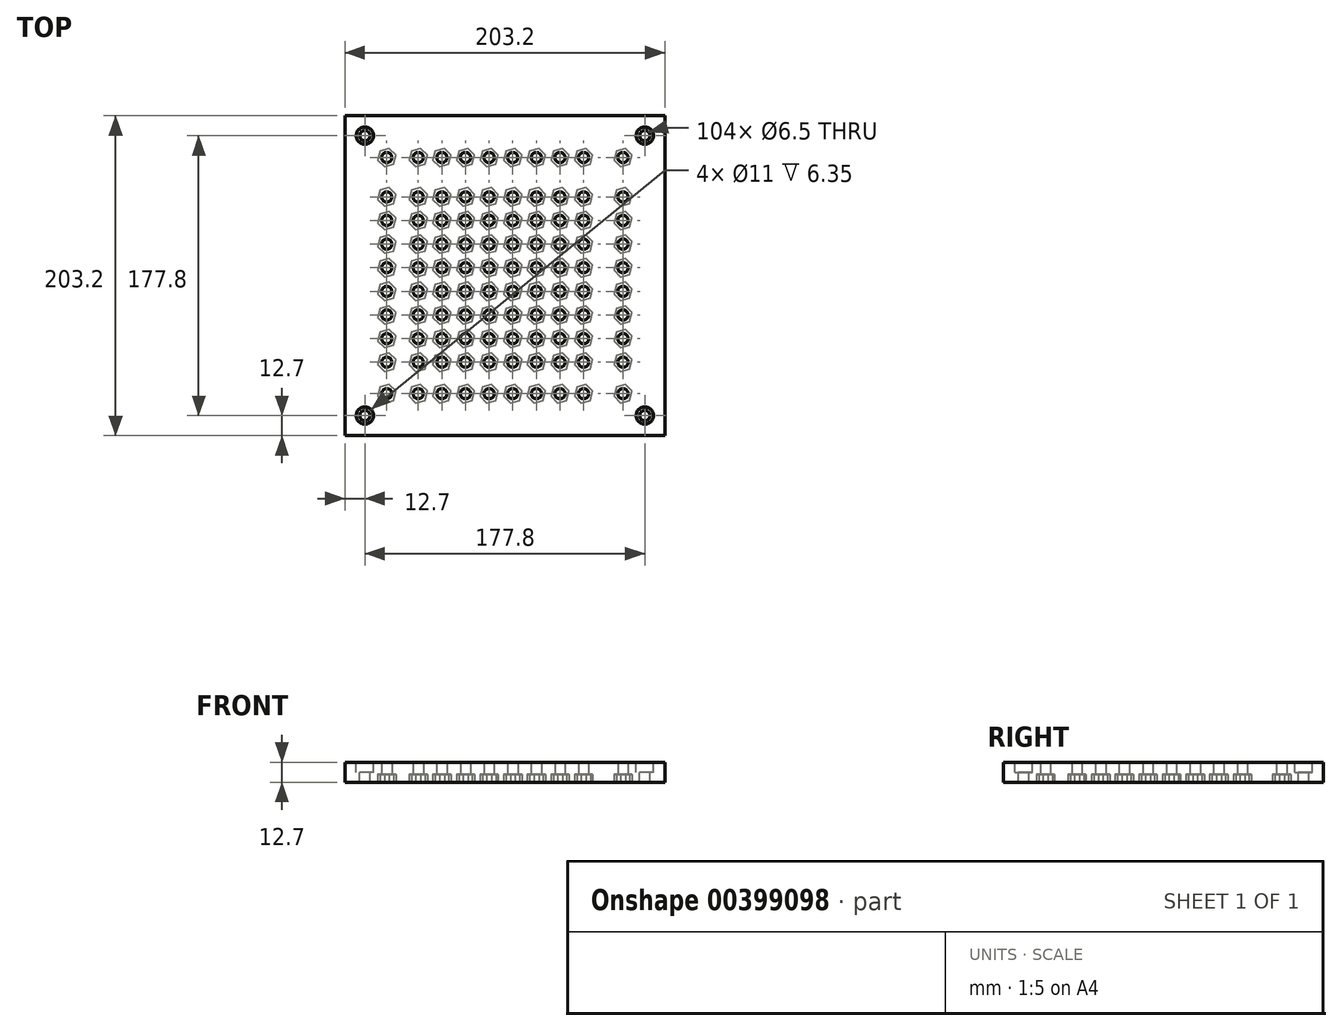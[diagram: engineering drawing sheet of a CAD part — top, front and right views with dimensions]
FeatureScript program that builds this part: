
annotation { "Feature Type Name" : "Feature", "Feature Type Description" : "" }
export const myFeature = defineFeature(function(context is Context, id is Id, definition is map)
    precondition{}
    {
        {
            assignVariable(context, id + "F0", {"name" : "M6NutThickness", "anyValue" : 5 * mm});
        }
        {
            var Q0;
            Q0=qCreatedBy(makeId("Top.planeOp"),FACE);
            var sketch = newSketch(context, id + "F1", { "sketchPlane" : qUnion([Q0])});
            skLineSegment(sketch, "E0.bottom", {"start": v(0, 0) * mm, "end": v(203.2, 0) * mm});
            skLineSegment(sketch, "E0.top", {"start": v(0, 203.2) * mm, "end": v(203.2, 203.2) * mm});
            skLineSegment(sketch, "E0.left", {"start": v(0, 0) * mm, "end": v(0, 203.2) * mm});
            skLineSegment(sketch, "E0.right", {"start": v(203.2, 0) * mm, "end": v(203.2, 203.2) * mm});
            skSolve(sketch);
        }
        {
            var Q0;
            Q0=makeQuery(id+"F1.imprint","IMPRINT",FACE,{"disambiguationData":[TD([[makeQuery(id+"F1.imprint","IMPRINT",EDGE,{"derivedFrom":sQuery(id+"F1.wireOp",EDGE,"E0.bottom")}),1.0]])]});
            extrude(context, id + "F2", {"entities" : qUnion([Q0]), "depth" : 12.7 * mm});
        }
        {
            var Q0;
            Q0=makeQuery(id+"F2.opExtrude","CAP_FACE",FACE,{"disambiguationData":[OSD([sQuery(id+"F1.wireOp",EDGE,"E0.bottom"),sQuery(id+"F1.wireOp",EDGE,"E0.top"),sQuery(id+"F1.wireOp",EDGE,"E0.left"),sQuery(id+"F1.wireOp",EDGE,"E0.right")])],"isStart":false});
            var sketch = newSketch(context, id + "F3", { "sketchPlane" : qUnion([Q0])});
            skCircle(sketch, "E1", {"center": v(12.7, 190.5) * mm, "radius": 5.5 * mm});
            skCircle(sketch, "E2", {"center": v(190.5, 190.5) * mm, "radius": 5.5 * mm});
            skCircle(sketch, "E3", {"center": v(190.5, 12.7) * mm, "radius": 5.5 * mm});
            skCircle(sketch, "E4", {"center": v(12.7, 12.7) * mm, "radius": 5.5 * mm});
            skCircle(sketch, "E5", {"center": v(12.7, 190.5) * mm, "radius": 3.25 * mm});
            skCircle(sketch, "E6", {"center": v(190.5, 190.5) * mm, "radius": 3.25 * mm});
            skCircle(sketch, "E7", {"center": v(190.5, 12.7) * mm, "radius": 3.25 * mm});
            skCircle(sketch, "E8", {"center": v(12.7, 12.7) * mm, "radius": 3.25 * mm});
            skSolve(sketch);
        }
        {
            var Q0;
            Q0=makeQuery(id+"F3.imprint","IMPRINT",FACE,{"disambiguationData":[TD([[makeQuery(id+"F3.imprint","IMPRINT",EDGE,{"derivedFrom":sQuery(id+"F3.wireOp",EDGE,"E1")}),1.0]])]});
            var Q1;
            Q1=makeQuery(id+"F3.imprint","IMPRINT",FACE,{"disambiguationData":[TD([[makeQuery(id+"F3.imprint","IMPRINT",EDGE,{"derivedFrom":sQuery(id+"F3.wireOp",EDGE,"E2")}),1.0]])]});
            var Q2;
            Q2=makeQuery(id+"F3.imprint","IMPRINT",FACE,{"disambiguationData":[TD([[makeQuery(id+"F3.imprint","IMPRINT",EDGE,{"derivedFrom":sQuery(id+"F3.wireOp",EDGE,"E3")}),1.0]])]});
            var Q3;
            Q3=makeQuery(id+"F3.imprint","IMPRINT",FACE,{"disambiguationData":[TD([[makeQuery(id+"F3.imprint","IMPRINT",EDGE,{"derivedFrom":sQuery(id+"F3.wireOp",EDGE,"E4")}),1.0]])]});
            var Q4;
            Q4=makeQuery(id+"F3.imprint","IMPRINT",FACE,{"disambiguationData":[TD([[makeQuery(id+"F3.imprint","IMPRINT",EDGE,{"derivedFrom":sQuery(id+"F3.wireOp",EDGE,"E5")}),1.0]])]});
            var Q5;
            Q5=makeQuery(id+"F3.imprint","IMPRINT",FACE,{"disambiguationData":[TD([[makeQuery(id+"F3.imprint","IMPRINT",EDGE,{"derivedFrom":sQuery(id+"F3.wireOp",EDGE,"ba32f473-7306-4966-8547-f8d374d792f3.0")}),-1.0]])]});
            var Q6;
            Q6=makeQuery(id+"F3.imprint","IMPRINT",FACE,{"disambiguationData":[TD([[makeQuery(id+"F3.imprint","IMPRINT",EDGE,{"derivedFrom":sQuery(id+"F3.wireOp",EDGE,"pHCyzxFQ-yNrH-yw88-MMIP-h8I6mzkWJt08")}),1.0]])]});
            var Q7;
            Q7=makeQuery(id+"F3.imprint","IMPRINT",FACE,{"disambiguationData":[TD([[makeQuery(id+"F3.imprint","IMPRINT",EDGE,{"derivedFrom":sQuery(id+"F3.wireOp",EDGE,"8c3efef8-5ac7-4a04-83c5-9b1e352e6b34")}),1.0]])]});
            var Q8;
            Q8=makeQuery(id+"F3.imprint","IMPRINT",FACE,{"disambiguationData":[TD([[makeQuery(id+"F3.imprint","IMPRINT",EDGE,{"derivedFrom":sQuery(id+"F3.wireOp",EDGE,"e6f48ea0-c1a9-460c-8d83-79fb5b6d435c.0")}),-1.0]])]});
            var Q9;
            Q9=makeQuery(id+"F3.imprint","IMPRINT",FACE,{"disambiguationData":[TD([[makeQuery(id+"F3.imprint","IMPRINT",EDGE,{"derivedFrom":sQuery(id+"F3.wireOp",EDGE,"E7")}),1.0]])]});
            var Q10;
            Q10=makeQuery(id+"F3.imprint","IMPRINT",FACE,{"disambiguationData":[TD([[makeQuery(id+"F3.imprint","IMPRINT",EDGE,{"derivedFrom":sQuery(id+"F3.wireOp",EDGE,"ca75a0d4-1ac4-49ba-8044-76483d581a22")}),1.0]])]});
            var Q11;
            Q11=makeQuery(id+"F3.imprint","IMPRINT",FACE,{"disambiguationData":[TD([[makeQuery(id+"F3.imprint","IMPRINT",EDGE,{"derivedFrom":sQuery(id+"F3.wireOp",EDGE,"484e9a5a-8a06-4af2-a13e-f69099c1e5a3.0")}),-1.0]])]});
            var Q12;
            Q12=makeQuery(id+"F3.imprint","IMPRINT",FACE,{"disambiguationData":[TD([[makeQuery(id+"F3.imprint","IMPRINT",EDGE,{"derivedFrom":sQuery(id+"F3.wireOp",EDGE,"0a7f3161-e935-40cb-8c32-bbe6e8a3d640.0")}),-1.0]])]});
            var Q13;
            Q13=makeQuery(id+"F3.imprint","IMPRINT",FACE,{"disambiguationData":[TD([[makeQuery(id+"F3.imprint","IMPRINT",EDGE,{"derivedFrom":sQuery(id+"F3.wireOp",EDGE,"f8818135-2c4b-4c98-9ffa-11e024e62321")}),1.0]])]});
            var Q14;
            Q14=makeQuery(id+"F3.imprint","IMPRINT",FACE,{"disambiguationData":[TD([[makeQuery(id+"F3.imprint","IMPRINT",EDGE,{"derivedFrom":sQuery(id+"F3.wireOp",EDGE,"3abde3a7-13fc-4790-a3ef-ddfa000d33fa")}),1.0]])]});
            var Q15;
            Q15=makeQuery(id+"F3.imprint","IMPRINT",FACE,{"disambiguationData":[TD([[makeQuery(id+"F3.imprint","IMPRINT",EDGE,{"derivedFrom":sQuery(id+"F3.wireOp",EDGE,"5478cdd5-5296-4cfe-a3e0-48035336e019.0")}),-1.0]])]});
            var Q16;
            Q16=makeQuery(id+"F3.imprint","IMPRINT",FACE,{"disambiguationData":[TD([[makeQuery(id+"F3.imprint","IMPRINT",EDGE,{"derivedFrom":sQuery(id+"F3.wireOp",EDGE,"bd25bac1-5707-4558-b08a-925dc677b274.0")}),-1.0]])]});
            var Q17;
            Q17=makeQuery(id+"F3.imprint","IMPRINT",FACE,{"disambiguationData":[TD([[makeQuery(id+"F3.imprint","IMPRINT",EDGE,{"derivedFrom":sQuery(id+"F3.wireOp",EDGE,"b3afb0ab-85e7-4117-a43b-624259399b40")}),1.0]])]});
            var Q18;
            Q18=makeQuery(id+"F3.imprint","IMPRINT",FACE,{"disambiguationData":[TD([[makeQuery(id+"F3.imprint","IMPRINT",EDGE,{"derivedFrom":sQuery(id+"F3.wireOp",EDGE,"E6")}),1.0]])]});
            var Q19;
            Q19=makeQuery(id+"F3.imprint","IMPRINT",FACE,{"disambiguationData":[TD([[makeQuery(id+"F3.imprint","IMPRINT",EDGE,{"derivedFrom":sQuery(id+"F3.wireOp",EDGE,"52d20c7e-8cc4-4a92-a8bc-447259732f1c")}),1.0]])]});
            var Q20;
            Q20=makeQuery(id+"F3.imprint","IMPRINT",FACE,{"disambiguationData":[TD([[makeQuery(id+"F3.imprint","IMPRINT",EDGE,{"derivedFrom":sQuery(id+"F3.wireOp",EDGE,"9f51e5bc-bef1-4550-8fb1-6146d32f1f4c.0")}),-1.0]])]});
            var Q21;
            Q21=makeQuery(id+"F3.imprint","IMPRINT",FACE,{"disambiguationData":[TD([[makeQuery(id+"F3.imprint","IMPRINT",EDGE,{"derivedFrom":sQuery(id+"F3.wireOp",EDGE,"a674802c-e204-4de5-9799-58b481744769")}),1.0]])]});
            var Q22;
            Q22=makeQuery(id+"F3.imprint","IMPRINT",FACE,{"disambiguationData":[TD([[makeQuery(id+"F3.imprint","IMPRINT",EDGE,{"derivedFrom":sQuery(id+"F3.wireOp",EDGE,"683618f0-5b4b-4870-9df9-abf6ab17f61a.0")}),-1.0]])]});
            var Q23;
            Q23=makeQuery(id+"F3.imprint","IMPRINT",FACE,{"disambiguationData":[TD([[makeQuery(id+"F3.imprint","IMPRINT",EDGE,{"derivedFrom":sQuery(id+"F3.wireOp",EDGE,"E8")}),1.0]])]});
            extrude(context, id + "F4", {"entities" : qUnion([Q0, Q1, Q2, Q3, Q4, Q5, Q6, Q7, Q8, Q9, Q10, Q11, Q12, Q13, Q14, Q15, Q16, Q17, Q18, Q19, Q20, Q21, Q22, Q23]), "operationType" : NewBodyOperationType.REMOVE, "oppositeDirection" : true, "depth" : 6.35 * mm});
        }
        {
            var Q0;
            Q0=makeQuery(id+"F3.imprint","IMPRINT",FACE,{"disambiguationData":[TD([[makeQuery(id+"F3.imprint","IMPRINT",EDGE,{"derivedFrom":sQuery(id+"F3.wireOp",EDGE,"E5")}),1.0]])]});
            var Q1;
            Q1=makeQuery(id+"F3.imprint","IMPRINT",FACE,{"disambiguationData":[TD([[makeQuery(id+"F3.imprint","IMPRINT",EDGE,{"derivedFrom":sQuery(id+"F3.wireOp",EDGE,"a674802c-e204-4de5-9799-58b481744769")}),1.0]])]});
            var Q2;
            Q2=makeQuery(id+"F3.imprint","IMPRINT",FACE,{"disambiguationData":[TD([[makeQuery(id+"F3.imprint","IMPRINT",EDGE,{"derivedFrom":sQuery(id+"F3.wireOp",EDGE,"52d20c7e-8cc4-4a92-a8bc-447259732f1c")}),1.0]])]});
            var Q3;
            Q3=makeQuery(id+"F3.imprint","IMPRINT",FACE,{"disambiguationData":[TD([[makeQuery(id+"F3.imprint","IMPRINT",EDGE,{"derivedFrom":sQuery(id+"F3.wireOp",EDGE,"E6")}),1.0]])]});
            var Q4;
            Q4=makeQuery(id+"F3.imprint","IMPRINT",FACE,{"disambiguationData":[TD([[makeQuery(id+"F3.imprint","IMPRINT",EDGE,{"derivedFrom":sQuery(id+"F3.wireOp",EDGE,"b3afb0ab-85e7-4117-a43b-624259399b40")}),1.0]])]});
            var Q5;
            Q5=makeQuery(id+"F3.imprint","IMPRINT",FACE,{"disambiguationData":[TD([[makeQuery(id+"F3.imprint","IMPRINT",EDGE,{"derivedFrom":sQuery(id+"F3.wireOp",EDGE,"3abde3a7-13fc-4790-a3ef-ddfa000d33fa")}),1.0]])]});
            var Q6;
            Q6=makeQuery(id+"F3.imprint","IMPRINT",FACE,{"disambiguationData":[TD([[makeQuery(id+"F3.imprint","IMPRINT",EDGE,{"derivedFrom":sQuery(id+"F3.wireOp",EDGE,"f8818135-2c4b-4c98-9ffa-11e024e62321")}),1.0]])]});
            var Q7;
            Q7=makeQuery(id+"F3.imprint","IMPRINT",FACE,{"disambiguationData":[TD([[makeQuery(id+"F3.imprint","IMPRINT",EDGE,{"derivedFrom":sQuery(id+"F3.wireOp",EDGE,"E7")}),1.0]])]});
            var Q8;
            Q8=makeQuery(id+"F3.imprint","IMPRINT",FACE,{"disambiguationData":[TD([[makeQuery(id+"F3.imprint","IMPRINT",EDGE,{"derivedFrom":sQuery(id+"F3.wireOp",EDGE,"ca75a0d4-1ac4-49ba-8044-76483d581a22")}),1.0]])]});
            var Q9;
            Q9=makeQuery(id+"F3.imprint","IMPRINT",FACE,{"disambiguationData":[TD([[makeQuery(id+"F3.imprint","IMPRINT",EDGE,{"derivedFrom":sQuery(id+"F3.wireOp",EDGE,"8c3efef8-5ac7-4a04-83c5-9b1e352e6b34")}),1.0]])]});
            var Q10;
            Q10=makeQuery(id+"F3.imprint","IMPRINT",FACE,{"disambiguationData":[TD([[makeQuery(id+"F3.imprint","IMPRINT",EDGE,{"derivedFrom":sQuery(id+"F3.wireOp",EDGE,"pHCyzxFQ-yNrH-yw88-MMIP-h8I6mzkWJt08")}),1.0]])]});
            var Q11;
            Q11=makeQuery(id+"F3.imprint","IMPRINT",FACE,{"disambiguationData":[TD([[makeQuery(id+"F3.imprint","IMPRINT",EDGE,{"derivedFrom":sQuery(id+"F3.wireOp",EDGE,"E8")}),1.0]])]});
            var Q12;
            Q12=makeQuery(id+"F2.opExtrude","CAP_FACE",FACE,{"disambiguationData":[OSD([sQuery(id+"F1.wireOp",EDGE,"E0.bottom"),sQuery(id+"F1.wireOp",EDGE,"E0.top"),sQuery(id+"F1.wireOp",EDGE,"E0.left"),sQuery(id+"F1.wireOp",EDGE,"E0.right")])],"isStart":true});
            extrude(context, id + "F5", {"entities" : qUnion([Q0, Q1, Q2, Q3, Q4, Q5, Q6, Q7, Q8, Q9, Q10, Q11]), "operationType" : NewBodyOperationType.REMOVE, "endBound" : BoundingType.THROUGH_ALL, "oppositeDirection" : true, "endBoundEntityFace" : qUnion([Q12]), "depth" : 25 * mm});
        }
        {
            var Q0;
            Q0=makeQuery(id+"F2.opExtrude","CAP_FACE",FACE,{"disambiguationData":[OSD([sQuery(id+"F1.wireOp",EDGE,"E0.bottom"),sQuery(id+"F1.wireOp",EDGE,"E0.top"),sQuery(id+"F1.wireOp",EDGE,"E0.left"),sQuery(id+"F1.wireOp",EDGE,"E0.right")])],"isStart":true});
            var sketch = newSketch(context, id + "F6", { "sketchPlane" : qUnion([Q0])});
            skCircle(sketch, "E9.cCircle", {"center": v(26.6, -26.6) * mm, "radius": 5.2 * mm, "construction": true});
            skLineSegment(sketch, "E9.0", {"start": v(25.05, -20.8) * mm, "end": v(30.85, -22.35) * mm});
            skLineSegment(sketch, "E9.1", {"start": v(30.85, -22.35) * mm, "end": v(32.4, -28.15) * mm});
            skLineSegment(sketch, "E9.2", {"start": v(32.4, -28.15) * mm, "end": v(28.15, -32.4) * mm});
            skLineSegment(sketch, "E9.3", {"start": v(28.15, -32.4) * mm, "end": v(22.35, -30.85) * mm});
            skLineSegment(sketch, "E9.4", {"start": v(22.35, -30.85) * mm, "end": v(20.8, -25.05) * mm});
            skLineSegment(sketch, "E9.5", {"start": v(20.8, -25.05) * mm, "end": v(25.05, -20.8) * mm});
            skPoint(sketch, "E9.0.midPoint", {"position": v(27.95, -21.58) * mm});
            skLineSegment(sketch, "E10", {"start": v(27.95, -21.58) * mm, "end": v(26.6, -26.6) * mm, "construction": true});
            skLineSegment(sketch, "E11", {"start": v(26.6, -21.4) * mm, "end": v(26.6, -26.6) * mm, "construction": true});
            skCircle(sketch, "E12", {"center": v(26.6, -26.6) * mm, "radius": 3.25 * mm});
            skCircle(sketch, "E13.cCircle", {"center": v(46.6, -26.6) * mm, "radius": 5.2 * mm, "construction": true});
            skLineSegment(sketch, "E13.0", {"start": v(45.05, -20.8) * mm, "end": v(50.85, -22.35) * mm});
            skLineSegment(sketch, "E13.1", {"start": v(50.85, -22.35) * mm, "end": v(52.4, -28.15) * mm});
            skLineSegment(sketch, "E13.2", {"start": v(52.4, -28.15) * mm, "end": v(48.15, -32.4) * mm});
            skLineSegment(sketch, "E13.3", {"start": v(48.15, -32.4) * mm, "end": v(42.35, -30.85) * mm});
            skLineSegment(sketch, "E13.4", {"start": v(42.35, -30.85) * mm, "end": v(40.8, -25.05) * mm});
            skLineSegment(sketch, "E13.5", {"start": v(40.8, -25.05) * mm, "end": v(45.05, -20.8) * mm});
            skPoint(sketch, "E13.0.midPoint", {"position": v(47.95, -21.58) * mm});
            skLineSegment(sketch, "E14", {"start": v(47.95, -21.58) * mm, "end": v(46.6, -26.6) * mm, "construction": true});
            skLineSegment(sketch, "E15", {"start": v(46.6, -21.4) * mm, "end": v(46.6, -26.6) * mm, "construction": true});
            skCircle(sketch, "E16", {"center": v(46.6, -26.6) * mm, "radius": 3.25 * mm});
            skCircle(sketch, "E17.cCircle", {"center": v(61.6, -26.6) * mm, "radius": 5.2 * mm, "construction": true});
            skLineSegment(sketch, "E17.0", {"start": v(60.05, -20.8) * mm, "end": v(65.85, -22.35) * mm});
            skLineSegment(sketch, "E17.1", {"start": v(65.85, -22.35) * mm, "end": v(67.4, -28.15) * mm});
            skLineSegment(sketch, "E17.2", {"start": v(67.4, -28.15) * mm, "end": v(63.15, -32.4) * mm});
            skLineSegment(sketch, "E17.3", {"start": v(63.15, -32.4) * mm, "end": v(57.35, -30.85) * mm});
            skLineSegment(sketch, "E17.4", {"start": v(57.35, -30.85) * mm, "end": v(55.8, -25.05) * mm});
            skLineSegment(sketch, "E17.5", {"start": v(55.8, -25.05) * mm, "end": v(60.05, -20.8) * mm});
            skPoint(sketch, "E17.0.midPoint", {"position": v(62.95, -21.58) * mm});
            skLineSegment(sketch, "E18", {"start": v(62.95, -21.58) * mm, "end": v(61.6, -26.6) * mm, "construction": true});
            skLineSegment(sketch, "E19", {"start": v(61.6, -21.4) * mm, "end": v(61.6, -26.6) * mm, "construction": true});
            skCircle(sketch, "E20", {"center": v(61.6, -26.6) * mm, "radius": 3.25 * mm});
            skCircle(sketch, "E21.cCircle", {"center": v(76.6, -26.6) * mm, "radius": 5.2 * mm, "construction": true});
            skLineSegment(sketch, "E21.0", {"start": v(75.05, -20.8) * mm, "end": v(80.85, -22.35) * mm});
            skLineSegment(sketch, "E21.1", {"start": v(80.85, -22.35) * mm, "end": v(82.4, -28.15) * mm});
            skLineSegment(sketch, "E21.2", {"start": v(82.4, -28.15) * mm, "end": v(78.15, -32.4) * mm});
            skLineSegment(sketch, "E21.3", {"start": v(78.15, -32.4) * mm, "end": v(72.35, -30.85) * mm});
            skLineSegment(sketch, "E21.4", {"start": v(72.35, -30.85) * mm, "end": v(70.8, -25.05) * mm});
            skLineSegment(sketch, "E21.5", {"start": v(70.8, -25.05) * mm, "end": v(75.05, -20.8) * mm});
            skPoint(sketch, "E21.0.midPoint", {"position": v(77.95, -21.58) * mm});
            skLineSegment(sketch, "E22", {"start": v(77.95, -21.58) * mm, "end": v(76.6, -26.6) * mm, "construction": true});
            skLineSegment(sketch, "E23", {"start": v(76.6, -21.4) * mm, "end": v(76.6, -26.6) * mm, "construction": true});
            skCircle(sketch, "E24", {"center": v(76.6, -26.6) * mm, "radius": 3.25 * mm});
            skCircle(sketch, "E25.cCircle", {"center": v(91.6, -26.6) * mm, "radius": 5.2 * mm, "construction": true});
            skLineSegment(sketch, "E25.0", {"start": v(90.05, -20.8) * mm, "end": v(95.85, -22.35) * mm});
            skLineSegment(sketch, "E25.1", {"start": v(95.85, -22.35) * mm, "end": v(97.4, -28.15) * mm});
            skLineSegment(sketch, "E25.2", {"start": v(97.4, -28.15) * mm, "end": v(93.15, -32.4) * mm});
            skLineSegment(sketch, "E25.3", {"start": v(93.15, -32.4) * mm, "end": v(87.35, -30.85) * mm});
            skLineSegment(sketch, "E25.4", {"start": v(87.35, -30.85) * mm, "end": v(85.8, -25.05) * mm});
            skLineSegment(sketch, "E25.5", {"start": v(85.8, -25.05) * mm, "end": v(90.05, -20.8) * mm});
            skPoint(sketch, "E25.0.midPoint", {"position": v(92.95, -21.58) * mm});
            skLineSegment(sketch, "E26", {"start": v(92.95, -21.58) * mm, "end": v(91.6, -26.6) * mm, "construction": true});
            skLineSegment(sketch, "E27", {"start": v(91.6, -21.4) * mm, "end": v(91.6, -26.6) * mm, "construction": true});
            skCircle(sketch, "E28", {"center": v(91.6, -26.6) * mm, "radius": 3.25 * mm});
            skCircle(sketch, "E29.cCircle", {"center": v(106.6, -26.6) * mm, "radius": 5.2 * mm, "construction": true});
            skLineSegment(sketch, "E29.0", {"start": v(105.05, -20.8) * mm, "end": v(110.85, -22.35) * mm});
            skLineSegment(sketch, "E29.1", {"start": v(110.85, -22.35) * mm, "end": v(112.4, -28.15) * mm});
            skLineSegment(sketch, "E29.2", {"start": v(112.4, -28.15) * mm, "end": v(108.15, -32.4) * mm});
            skLineSegment(sketch, "E29.3", {"start": v(108.15, -32.4) * mm, "end": v(102.35, -30.85) * mm});
            skLineSegment(sketch, "E29.4", {"start": v(102.35, -30.85) * mm, "end": v(100.8, -25.05) * mm});
            skLineSegment(sketch, "E29.5", {"start": v(100.8, -25.05) * mm, "end": v(105.05, -20.8) * mm});
            skPoint(sketch, "E29.0.midPoint", {"position": v(107.95, -21.58) * mm});
            skLineSegment(sketch, "E30", {"start": v(107.95, -21.58) * mm, "end": v(106.6, -26.6) * mm, "construction": true});
            skLineSegment(sketch, "E31", {"start": v(106.6, -21.4) * mm, "end": v(106.6, -26.6) * mm, "construction": true});
            skCircle(sketch, "E32", {"center": v(106.6, -26.6) * mm, "radius": 3.25 * mm});
            skCircle(sketch, "E33.cCircle", {"center": v(121.6, -26.6) * mm, "radius": 5.2 * mm, "construction": true});
            skLineSegment(sketch, "E33.0", {"start": v(120.05, -20.8) * mm, "end": v(125.85, -22.35) * mm});
            skLineSegment(sketch, "E33.1", {"start": v(125.85, -22.35) * mm, "end": v(127.4, -28.15) * mm});
            skLineSegment(sketch, "E33.2", {"start": v(127.4, -28.15) * mm, "end": v(123.15, -32.4) * mm});
            skLineSegment(sketch, "E33.3", {"start": v(123.15, -32.4) * mm, "end": v(117.35, -30.85) * mm});
            skLineSegment(sketch, "E33.4", {"start": v(117.35, -30.85) * mm, "end": v(115.8, -25.05) * mm});
            skLineSegment(sketch, "E33.5", {"start": v(115.8, -25.05) * mm, "end": v(120.05, -20.8) * mm});
            skPoint(sketch, "E33.0.midPoint", {"position": v(122.95, -21.58) * mm});
            skLineSegment(sketch, "E34", {"start": v(122.95, -21.58) * mm, "end": v(121.6, -26.6) * mm, "construction": true});
            skLineSegment(sketch, "E35", {"start": v(121.6, -21.4) * mm, "end": v(121.6, -26.6) * mm, "construction": true});
            skCircle(sketch, "E36", {"center": v(121.6, -26.6) * mm, "radius": 3.25 * mm});
            skCircle(sketch, "E37.cCircle", {"center": v(136.6, -26.6) * mm, "radius": 5.2 * mm, "construction": true});
            skLineSegment(sketch, "E37.0", {"start": v(135.05, -20.8) * mm, "end": v(140.85, -22.35) * mm});
            skLineSegment(sketch, "E37.1", {"start": v(140.85, -22.35) * mm, "end": v(142.4, -28.15) * mm});
            skLineSegment(sketch, "E37.2", {"start": v(142.4, -28.15) * mm, "end": v(138.15, -32.4) * mm});
            skLineSegment(sketch, "E37.3", {"start": v(138.15, -32.4) * mm, "end": v(132.35, -30.85) * mm});
            skLineSegment(sketch, "E37.4", {"start": v(132.35, -30.85) * mm, "end": v(130.8, -25.05) * mm});
            skLineSegment(sketch, "E37.5", {"start": v(130.8, -25.05) * mm, "end": v(135.05, -20.8) * mm});
            skPoint(sketch, "E37.0.midPoint", {"position": v(137.95, -21.58) * mm});
            skLineSegment(sketch, "E38", {"start": v(137.95, -21.58) * mm, "end": v(136.6, -26.6) * mm, "construction": true});
            skLineSegment(sketch, "E39", {"start": v(136.6, -21.4) * mm, "end": v(136.6, -26.6) * mm, "construction": true});
            skCircle(sketch, "E40", {"center": v(136.6, -26.6) * mm, "radius": 3.25 * mm});
            skCircle(sketch, "E41.cCircle", {"center": v(151.6, -26.6) * mm, "radius": 5.2 * mm, "construction": true});
            skLineSegment(sketch, "E41.0", {"start": v(150.05, -20.8) * mm, "end": v(155.85, -22.35) * mm});
            skLineSegment(sketch, "E41.1", {"start": v(155.85, -22.35) * mm, "end": v(157.4, -28.15) * mm});
            skLineSegment(sketch, "E41.2", {"start": v(157.4, -28.15) * mm, "end": v(153.15, -32.4) * mm});
            skLineSegment(sketch, "E41.3", {"start": v(153.15, -32.4) * mm, "end": v(147.35, -30.85) * mm});
            skLineSegment(sketch, "E41.4", {"start": v(147.35, -30.85) * mm, "end": v(145.8, -25.05) * mm});
            skLineSegment(sketch, "E41.5", {"start": v(145.8, -25.05) * mm, "end": v(150.05, -20.8) * mm});
            skPoint(sketch, "E41.0.midPoint", {"position": v(152.95, -21.58) * mm});
            skLineSegment(sketch, "E42", {"start": v(152.95, -21.58) * mm, "end": v(151.6, -26.6) * mm, "construction": true});
            skLineSegment(sketch, "E43", {"start": v(151.6, -21.4) * mm, "end": v(151.6, -26.6) * mm, "construction": true});
            skCircle(sketch, "E44", {"center": v(151.6, -26.6) * mm, "radius": 3.25 * mm});
            skCircle(sketch, "E45.cCircle", {"center": v(176.6, -26.6) * mm, "radius": 5.2 * mm, "construction": true});
            skLineSegment(sketch, "E45.0", {"start": v(175.05, -20.8) * mm, "end": v(180.85, -22.35) * mm});
            skLineSegment(sketch, "E45.1", {"start": v(180.85, -22.35) * mm, "end": v(182.4, -28.15) * mm});
            skLineSegment(sketch, "E45.2", {"start": v(182.4, -28.15) * mm, "end": v(178.15, -32.4) * mm});
            skLineSegment(sketch, "E45.3", {"start": v(178.15, -32.4) * mm, "end": v(172.35, -30.85) * mm});
            skLineSegment(sketch, "E45.4", {"start": v(172.35, -30.85) * mm, "end": v(170.8, -25.05) * mm});
            skLineSegment(sketch, "E45.5", {"start": v(170.8, -25.05) * mm, "end": v(175.05, -20.8) * mm});
            skPoint(sketch, "E45.0.midPoint", {"position": v(177.95, -21.58) * mm});
            skLineSegment(sketch, "E46", {"start": v(177.95, -21.58) * mm, "end": v(176.6, -26.6) * mm, "construction": true});
            skLineSegment(sketch, "E47", {"start": v(176.6, -21.4) * mm, "end": v(176.6, -26.6) * mm, "construction": true});
            skCircle(sketch, "E48", {"center": v(176.6, -26.6) * mm, "radius": 3.25 * mm});
            skCircle(sketch, "E49.cCircle", {"center": v(26.6, -46.6) * mm, "radius": 5.2 * mm, "construction": true});
            skLineSegment(sketch, "E49.0", {"start": v(25.05, -40.8) * mm, "end": v(30.85, -42.35) * mm});
            skLineSegment(sketch, "E49.1", {"start": v(30.85, -42.35) * mm, "end": v(32.4, -48.15) * mm});
            skLineSegment(sketch, "E49.2", {"start": v(32.4, -48.15) * mm, "end": v(28.15, -52.4) * mm});
            skLineSegment(sketch, "E49.3", {"start": v(28.15, -52.4) * mm, "end": v(22.35, -50.85) * mm});
            skLineSegment(sketch, "E49.4", {"start": v(22.35, -50.85) * mm, "end": v(20.8, -45.05) * mm});
            skLineSegment(sketch, "E49.5", {"start": v(20.8, -45.05) * mm, "end": v(25.05, -40.8) * mm});
            skPoint(sketch, "E49.0.midPoint", {"position": v(27.95, -41.58) * mm});
            skLineSegment(sketch, "E50", {"start": v(27.95, -41.58) * mm, "end": v(26.6, -46.6) * mm, "construction": true});
            skLineSegment(sketch, "E51", {"start": v(26.6, -41.4) * mm, "end": v(26.6, -46.6) * mm, "construction": true});
            skCircle(sketch, "E52", {"center": v(26.6, -46.6) * mm, "radius": 3.25 * mm});
            skCircle(sketch, "E53.cCircle", {"center": v(46.6, -46.6) * mm, "radius": 5.2 * mm, "construction": true});
            skLineSegment(sketch, "E53.0", {"start": v(45.05, -40.8) * mm, "end": v(50.85, -42.35) * mm});
            skLineSegment(sketch, "E53.1", {"start": v(50.85, -42.35) * mm, "end": v(52.4, -48.15) * mm});
            skLineSegment(sketch, "E53.2", {"start": v(52.4, -48.15) * mm, "end": v(48.15, -52.4) * mm});
            skLineSegment(sketch, "E53.3", {"start": v(48.15, -52.4) * mm, "end": v(42.35, -50.85) * mm});
            skLineSegment(sketch, "E53.4", {"start": v(42.35, -50.85) * mm, "end": v(40.8, -45.05) * mm});
            skLineSegment(sketch, "E53.5", {"start": v(40.8, -45.05) * mm, "end": v(45.05, -40.8) * mm});
            skPoint(sketch, "E53.0.midPoint", {"position": v(47.95, -41.58) * mm});
            skLineSegment(sketch, "E54", {"start": v(47.95, -41.58) * mm, "end": v(46.6, -46.6) * mm, "construction": true});
            skLineSegment(sketch, "E55", {"start": v(46.6, -41.4) * mm, "end": v(46.6, -46.6) * mm, "construction": true});
            skCircle(sketch, "E56", {"center": v(46.6, -46.6) * mm, "radius": 3.25 * mm});
            skCircle(sketch, "E57.cCircle", {"center": v(61.6, -46.6) * mm, "radius": 5.2 * mm, "construction": true});
            skLineSegment(sketch, "E57.0", {"start": v(60.05, -40.8) * mm, "end": v(65.85, -42.35) * mm});
            skLineSegment(sketch, "E57.1", {"start": v(65.85, -42.35) * mm, "end": v(67.4, -48.15) * mm});
            skLineSegment(sketch, "E57.2", {"start": v(67.4, -48.15) * mm, "end": v(63.15, -52.4) * mm});
            skLineSegment(sketch, "E57.3", {"start": v(63.15, -52.4) * mm, "end": v(57.35, -50.85) * mm});
            skLineSegment(sketch, "E57.4", {"start": v(57.35, -50.85) * mm, "end": v(55.8, -45.05) * mm});
            skLineSegment(sketch, "E57.5", {"start": v(55.8, -45.05) * mm, "end": v(60.05, -40.8) * mm});
            skPoint(sketch, "E57.0.midPoint", {"position": v(62.95, -41.58) * mm});
            skLineSegment(sketch, "E58", {"start": v(62.95, -41.58) * mm, "end": v(61.6, -46.6) * mm, "construction": true});
            skLineSegment(sketch, "E59", {"start": v(61.6, -41.4) * mm, "end": v(61.6, -46.6) * mm, "construction": true});
            skCircle(sketch, "E60", {"center": v(61.6, -46.6) * mm, "radius": 3.25 * mm});
            skCircle(sketch, "E61.cCircle", {"center": v(76.6, -46.6) * mm, "radius": 5.2 * mm, "construction": true});
            skLineSegment(sketch, "E61.0", {"start": v(75.05, -40.8) * mm, "end": v(80.85, -42.35) * mm});
            skLineSegment(sketch, "E61.1", {"start": v(80.85, -42.35) * mm, "end": v(82.4, -48.15) * mm});
            skLineSegment(sketch, "E61.2", {"start": v(82.4, -48.15) * mm, "end": v(78.15, -52.4) * mm});
            skLineSegment(sketch, "E61.3", {"start": v(78.15, -52.4) * mm, "end": v(72.35, -50.85) * mm});
            skLineSegment(sketch, "E61.4", {"start": v(72.35, -50.85) * mm, "end": v(70.8, -45.05) * mm});
            skLineSegment(sketch, "E61.5", {"start": v(70.8, -45.05) * mm, "end": v(75.05, -40.8) * mm});
            skPoint(sketch, "E61.0.midPoint", {"position": v(77.95, -41.58) * mm});
            skLineSegment(sketch, "E62", {"start": v(77.95, -41.58) * mm, "end": v(76.6, -46.6) * mm, "construction": true});
            skLineSegment(sketch, "E63", {"start": v(76.6, -41.4) * mm, "end": v(76.6, -46.6) * mm, "construction": true});
            skCircle(sketch, "E64", {"center": v(76.6, -46.6) * mm, "radius": 3.25 * mm});
            skCircle(sketch, "E65.cCircle", {"center": v(91.6, -46.6) * mm, "radius": 5.2 * mm, "construction": true});
            skLineSegment(sketch, "E65.0", {"start": v(90.05, -40.8) * mm, "end": v(95.85, -42.35) * mm});
            skLineSegment(sketch, "E65.1", {"start": v(95.85, -42.35) * mm, "end": v(97.4, -48.15) * mm});
            skLineSegment(sketch, "E65.2", {"start": v(97.4, -48.15) * mm, "end": v(93.15, -52.4) * mm});
            skLineSegment(sketch, "E65.3", {"start": v(93.15, -52.4) * mm, "end": v(87.35, -50.85) * mm});
            skLineSegment(sketch, "E65.4", {"start": v(87.35, -50.85) * mm, "end": v(85.8, -45.05) * mm});
            skLineSegment(sketch, "E65.5", {"start": v(85.8, -45.05) * mm, "end": v(90.05, -40.8) * mm});
            skPoint(sketch, "E65.0.midPoint", {"position": v(92.95, -41.58) * mm});
            skLineSegment(sketch, "E66", {"start": v(92.95, -41.58) * mm, "end": v(91.6, -46.6) * mm, "construction": true});
            skLineSegment(sketch, "E67", {"start": v(91.6, -41.4) * mm, "end": v(91.6, -46.6) * mm, "construction": true});
            skCircle(sketch, "E68", {"center": v(91.6, -46.6) * mm, "radius": 3.25 * mm});
            skCircle(sketch, "E69.cCircle", {"center": v(106.6, -46.6) * mm, "radius": 5.2 * mm, "construction": true});
            skLineSegment(sketch, "E69.0", {"start": v(105.05, -40.8) * mm, "end": v(110.85, -42.35) * mm});
            skLineSegment(sketch, "E69.1", {"start": v(110.85, -42.35) * mm, "end": v(112.4, -48.15) * mm});
            skLineSegment(sketch, "E69.2", {"start": v(112.4, -48.15) * mm, "end": v(108.15, -52.4) * mm});
            skLineSegment(sketch, "E69.3", {"start": v(108.15, -52.4) * mm, "end": v(102.35, -50.85) * mm});
            skLineSegment(sketch, "E69.4", {"start": v(102.35, -50.85) * mm, "end": v(100.8, -45.05) * mm});
            skLineSegment(sketch, "E69.5", {"start": v(100.8, -45.05) * mm, "end": v(105.05, -40.8) * mm});
            skPoint(sketch, "E69.0.midPoint", {"position": v(107.95, -41.58) * mm});
            skLineSegment(sketch, "E70", {"start": v(107.95, -41.58) * mm, "end": v(106.6, -46.6) * mm, "construction": true});
            skLineSegment(sketch, "E71", {"start": v(106.6, -41.4) * mm, "end": v(106.6, -46.6) * mm, "construction": true});
            skCircle(sketch, "E72", {"center": v(106.6, -46.6) * mm, "radius": 3.25 * mm});
            skCircle(sketch, "E73.cCircle", {"center": v(121.6, -46.6) * mm, "radius": 5.2 * mm, "construction": true});
            skLineSegment(sketch, "E73.0", {"start": v(120.05, -40.8) * mm, "end": v(125.85, -42.35) * mm});
            skLineSegment(sketch, "E73.1", {"start": v(125.85, -42.35) * mm, "end": v(127.4, -48.15) * mm});
            skLineSegment(sketch, "E73.2", {"start": v(127.4, -48.15) * mm, "end": v(123.15, -52.4) * mm});
            skLineSegment(sketch, "E73.3", {"start": v(123.15, -52.4) * mm, "end": v(117.35, -50.85) * mm});
            skLineSegment(sketch, "E73.4", {"start": v(117.35, -50.85) * mm, "end": v(115.8, -45.05) * mm});
            skLineSegment(sketch, "E73.5", {"start": v(115.8, -45.05) * mm, "end": v(120.05, -40.8) * mm});
            skPoint(sketch, "E73.0.midPoint", {"position": v(122.95, -41.58) * mm});
            skLineSegment(sketch, "E74", {"start": v(122.95, -41.58) * mm, "end": v(121.6, -46.6) * mm, "construction": true});
            skLineSegment(sketch, "E75", {"start": v(121.6, -41.4) * mm, "end": v(121.6, -46.6) * mm, "construction": true});
            skCircle(sketch, "E76", {"center": v(121.6, -46.6) * mm, "radius": 3.25 * mm});
            skCircle(sketch, "E77.cCircle", {"center": v(136.6, -46.6) * mm, "radius": 5.2 * mm, "construction": true});
            skLineSegment(sketch, "E77.0", {"start": v(135.05, -40.8) * mm, "end": v(140.85, -42.35) * mm});
            skLineSegment(sketch, "E77.1", {"start": v(140.85, -42.35) * mm, "end": v(142.4, -48.15) * mm});
            skLineSegment(sketch, "E77.2", {"start": v(142.4, -48.15) * mm, "end": v(138.15, -52.4) * mm});
            skLineSegment(sketch, "E77.3", {"start": v(138.15, -52.4) * mm, "end": v(132.35, -50.85) * mm});
            skLineSegment(sketch, "E77.4", {"start": v(132.35, -50.85) * mm, "end": v(130.8, -45.05) * mm});
            skLineSegment(sketch, "E77.5", {"start": v(130.8, -45.05) * mm, "end": v(135.05, -40.8) * mm});
            skPoint(sketch, "E77.0.midPoint", {"position": v(137.95, -41.58) * mm});
            skLineSegment(sketch, "E78", {"start": v(137.95, -41.58) * mm, "end": v(136.6, -46.6) * mm, "construction": true});
            skLineSegment(sketch, "E79", {"start": v(136.6, -41.4) * mm, "end": v(136.6, -46.6) * mm, "construction": true});
            skCircle(sketch, "E80", {"center": v(136.6, -46.6) * mm, "radius": 3.25 * mm});
            skCircle(sketch, "E81.cCircle", {"center": v(151.6, -46.6) * mm, "radius": 5.2 * mm, "construction": true});
            skLineSegment(sketch, "E81.0", {"start": v(150.05, -40.8) * mm, "end": v(155.85, -42.35) * mm});
            skLineSegment(sketch, "E81.1", {"start": v(155.85, -42.35) * mm, "end": v(157.4, -48.15) * mm});
            skLineSegment(sketch, "E81.2", {"start": v(157.4, -48.15) * mm, "end": v(153.15, -52.4) * mm});
            skLineSegment(sketch, "E81.3", {"start": v(153.15, -52.4) * mm, "end": v(147.35, -50.85) * mm});
            skLineSegment(sketch, "E81.4", {"start": v(147.35, -50.85) * mm, "end": v(145.8, -45.05) * mm});
            skLineSegment(sketch, "E81.5", {"start": v(145.8, -45.05) * mm, "end": v(150.05, -40.8) * mm});
            skPoint(sketch, "E81.0.midPoint", {"position": v(152.95, -41.58) * mm});
            skLineSegment(sketch, "E82", {"start": v(152.95, -41.58) * mm, "end": v(151.6, -46.6) * mm, "construction": true});
            skLineSegment(sketch, "E83", {"start": v(151.6, -41.4) * mm, "end": v(151.6, -46.6) * mm, "construction": true});
            skCircle(sketch, "E84", {"center": v(151.6, -46.6) * mm, "radius": 3.25 * mm});
            skCircle(sketch, "E85.cCircle", {"center": v(176.6, -46.6) * mm, "radius": 5.2 * mm, "construction": true});
            skLineSegment(sketch, "E85.0", {"start": v(175.05, -40.8) * mm, "end": v(180.85, -42.35) * mm});
            skLineSegment(sketch, "E85.1", {"start": v(180.85, -42.35) * mm, "end": v(182.4, -48.15) * mm});
            skLineSegment(sketch, "E85.2", {"start": v(182.4, -48.15) * mm, "end": v(178.15, -52.4) * mm});
            skLineSegment(sketch, "E85.3", {"start": v(178.15, -52.4) * mm, "end": v(172.35, -50.85) * mm});
            skLineSegment(sketch, "E85.4", {"start": v(172.35, -50.85) * mm, "end": v(170.8, -45.05) * mm});
            skLineSegment(sketch, "E85.5", {"start": v(170.8, -45.05) * mm, "end": v(175.05, -40.8) * mm});
            skPoint(sketch, "E85.0.midPoint", {"position": v(177.95, -41.58) * mm});
            skLineSegment(sketch, "E86", {"start": v(177.95, -41.58) * mm, "end": v(176.6, -46.6) * mm, "construction": true});
            skLineSegment(sketch, "E87", {"start": v(176.6, -41.4) * mm, "end": v(176.6, -46.6) * mm, "construction": true});
            skCircle(sketch, "E88", {"center": v(176.6, -46.6) * mm, "radius": 3.25 * mm});
            skCircle(sketch, "E89.cCircle", {"center": v(26.6, -61.6) * mm, "radius": 5.2 * mm, "construction": true});
            skLineSegment(sketch, "E89.0", {"start": v(25.05, -55.8) * mm, "end": v(30.85, -57.35) * mm});
            skLineSegment(sketch, "E89.1", {"start": v(30.85, -57.35) * mm, "end": v(32.4, -63.15) * mm});
            skLineSegment(sketch, "E89.2", {"start": v(32.4, -63.15) * mm, "end": v(28.15, -67.4) * mm});
            skLineSegment(sketch, "E89.3", {"start": v(28.15, -67.4) * mm, "end": v(22.35, -65.85) * mm});
            skLineSegment(sketch, "E89.4", {"start": v(22.35, -65.85) * mm, "end": v(20.8, -60.05) * mm});
            skLineSegment(sketch, "E89.5", {"start": v(20.8, -60.05) * mm, "end": v(25.05, -55.8) * mm});
            skPoint(sketch, "E89.0.midPoint", {"position": v(27.95, -56.58) * mm});
            skLineSegment(sketch, "E90", {"start": v(27.95, -56.58) * mm, "end": v(26.6, -61.6) * mm, "construction": true});
            skLineSegment(sketch, "E91", {"start": v(26.6, -56.4) * mm, "end": v(26.6, -61.6) * mm, "construction": true});
            skCircle(sketch, "E92", {"center": v(26.6, -61.6) * mm, "radius": 3.25 * mm});
            skCircle(sketch, "E93.cCircle", {"center": v(46.6, -61.6) * mm, "radius": 5.2 * mm, "construction": true});
            skLineSegment(sketch, "E93.0", {"start": v(45.05, -55.8) * mm, "end": v(50.85, -57.35) * mm});
            skLineSegment(sketch, "E93.1", {"start": v(50.85, -57.35) * mm, "end": v(52.4, -63.15) * mm});
            skLineSegment(sketch, "E93.2", {"start": v(52.4, -63.15) * mm, "end": v(48.15, -67.4) * mm});
            skLineSegment(sketch, "E93.3", {"start": v(48.15, -67.4) * mm, "end": v(42.35, -65.85) * mm});
            skLineSegment(sketch, "E93.4", {"start": v(42.35, -65.85) * mm, "end": v(40.8, -60.05) * mm});
            skLineSegment(sketch, "E93.5", {"start": v(40.8, -60.05) * mm, "end": v(45.05, -55.8) * mm});
            skPoint(sketch, "E93.0.midPoint", {"position": v(47.95, -56.58) * mm});
            skLineSegment(sketch, "E94", {"start": v(47.95, -56.58) * mm, "end": v(46.6, -61.6) * mm, "construction": true});
            skLineSegment(sketch, "E95", {"start": v(46.6, -56.4) * mm, "end": v(46.6, -61.6) * mm, "construction": true});
            skCircle(sketch, "E96", {"center": v(46.6, -61.6) * mm, "radius": 3.25 * mm});
            skCircle(sketch, "E97.cCircle", {"center": v(61.6, -61.6) * mm, "radius": 5.2 * mm, "construction": true});
            skLineSegment(sketch, "E97.0", {"start": v(60.05, -55.8) * mm, "end": v(65.85, -57.35) * mm});
            skLineSegment(sketch, "E97.1", {"start": v(65.85, -57.35) * mm, "end": v(67.4, -63.15) * mm});
            skLineSegment(sketch, "E97.2", {"start": v(67.4, -63.15) * mm, "end": v(63.15, -67.4) * mm});
            skLineSegment(sketch, "E97.3", {"start": v(63.15, -67.4) * mm, "end": v(57.35, -65.85) * mm});
            skLineSegment(sketch, "E97.4", {"start": v(57.35, -65.85) * mm, "end": v(55.8, -60.05) * mm});
            skLineSegment(sketch, "E97.5", {"start": v(55.8, -60.05) * mm, "end": v(60.05, -55.8) * mm});
            skPoint(sketch, "E97.0.midPoint", {"position": v(62.95, -56.58) * mm});
            skLineSegment(sketch, "E98", {"start": v(62.95, -56.58) * mm, "end": v(61.6, -61.6) * mm, "construction": true});
            skLineSegment(sketch, "E99", {"start": v(61.6, -56.4) * mm, "end": v(61.6, -61.6) * mm, "construction": true});
            skCircle(sketch, "E100", {"center": v(61.6, -61.6) * mm, "radius": 3.25 * mm});
            skCircle(sketch, "E101.cCircle", {"center": v(76.6, -61.6) * mm, "radius": 5.2 * mm, "construction": true});
            skLineSegment(sketch, "E101.0", {"start": v(75.05, -55.8) * mm, "end": v(80.85, -57.35) * mm});
            skLineSegment(sketch, "E101.1", {"start": v(80.85, -57.35) * mm, "end": v(82.4, -63.15) * mm});
            skLineSegment(sketch, "E101.2", {"start": v(82.4, -63.15) * mm, "end": v(78.15, -67.4) * mm});
            skLineSegment(sketch, "E101.3", {"start": v(78.15, -67.4) * mm, "end": v(72.35, -65.85) * mm});
            skLineSegment(sketch, "E101.4", {"start": v(72.35, -65.85) * mm, "end": v(70.8, -60.05) * mm});
            skLineSegment(sketch, "E101.5", {"start": v(70.8, -60.05) * mm, "end": v(75.05, -55.8) * mm});
            skPoint(sketch, "E101.0.midPoint", {"position": v(77.95, -56.58) * mm});
            skLineSegment(sketch, "E102", {"start": v(77.95, -56.58) * mm, "end": v(76.6, -61.6) * mm, "construction": true});
            skLineSegment(sketch, "E103", {"start": v(76.6, -56.4) * mm, "end": v(76.6, -61.6) * mm, "construction": true});
            skCircle(sketch, "E104", {"center": v(76.6, -61.6) * mm, "radius": 3.25 * mm});
            skCircle(sketch, "E105.cCircle", {"center": v(91.6, -61.6) * mm, "radius": 5.2 * mm, "construction": true});
            skLineSegment(sketch, "E105.0", {"start": v(90.05, -55.8) * mm, "end": v(95.85, -57.35) * mm});
            skLineSegment(sketch, "E105.1", {"start": v(95.85, -57.35) * mm, "end": v(97.4, -63.15) * mm});
            skLineSegment(sketch, "E105.2", {"start": v(97.4, -63.15) * mm, "end": v(93.15, -67.4) * mm});
            skLineSegment(sketch, "E105.3", {"start": v(93.15, -67.4) * mm, "end": v(87.35, -65.85) * mm});
            skLineSegment(sketch, "E105.4", {"start": v(87.35, -65.85) * mm, "end": v(85.8, -60.05) * mm});
            skLineSegment(sketch, "E105.5", {"start": v(85.8, -60.05) * mm, "end": v(90.05, -55.8) * mm});
            skPoint(sketch, "E105.0.midPoint", {"position": v(92.95, -56.58) * mm});
            skLineSegment(sketch, "E106", {"start": v(92.95, -56.58) * mm, "end": v(91.6, -61.6) * mm, "construction": true});
            skLineSegment(sketch, "E107", {"start": v(91.6, -56.4) * mm, "end": v(91.6, -61.6) * mm, "construction": true});
            skCircle(sketch, "E108", {"center": v(91.6, -61.6) * mm, "radius": 3.25 * mm});
            skCircle(sketch, "E109.cCircle", {"center": v(106.6, -61.6) * mm, "radius": 5.2 * mm, "construction": true});
            skLineSegment(sketch, "E109.0", {"start": v(105.05, -55.8) * mm, "end": v(110.85, -57.35) * mm});
            skLineSegment(sketch, "E109.1", {"start": v(110.85, -57.35) * mm, "end": v(112.4, -63.15) * mm});
            skLineSegment(sketch, "E109.2", {"start": v(112.4, -63.15) * mm, "end": v(108.15, -67.4) * mm});
            skLineSegment(sketch, "E109.3", {"start": v(108.15, -67.4) * mm, "end": v(102.35, -65.85) * mm});
            skLineSegment(sketch, "E109.4", {"start": v(102.35, -65.85) * mm, "end": v(100.8, -60.05) * mm});
            skLineSegment(sketch, "E109.5", {"start": v(100.8, -60.05) * mm, "end": v(105.05, -55.8) * mm});
            skPoint(sketch, "E109.0.midPoint", {"position": v(107.95, -56.58) * mm});
            skLineSegment(sketch, "E110", {"start": v(107.95, -56.58) * mm, "end": v(106.6, -61.6) * mm, "construction": true});
            skLineSegment(sketch, "E111", {"start": v(106.6, -56.4) * mm, "end": v(106.6, -61.6) * mm, "construction": true});
            skCircle(sketch, "E112", {"center": v(106.6, -61.6) * mm, "radius": 3.25 * mm});
            skCircle(sketch, "E113.cCircle", {"center": v(121.6, -61.6) * mm, "radius": 5.2 * mm, "construction": true});
            skLineSegment(sketch, "E113.0", {"start": v(120.05, -55.8) * mm, "end": v(125.85, -57.35) * mm});
            skLineSegment(sketch, "E113.1", {"start": v(125.85, -57.35) * mm, "end": v(127.4, -63.15) * mm});
            skLineSegment(sketch, "E113.2", {"start": v(127.4, -63.15) * mm, "end": v(123.15, -67.4) * mm});
            skLineSegment(sketch, "E113.3", {"start": v(123.15, -67.4) * mm, "end": v(117.35, -65.85) * mm});
            skLineSegment(sketch, "E113.4", {"start": v(117.35, -65.85) * mm, "end": v(115.8, -60.05) * mm});
            skLineSegment(sketch, "E113.5", {"start": v(115.8, -60.05) * mm, "end": v(120.05, -55.8) * mm});
            skPoint(sketch, "E113.0.midPoint", {"position": v(122.95, -56.58) * mm});
            skLineSegment(sketch, "E114", {"start": v(122.95, -56.58) * mm, "end": v(121.6, -61.6) * mm, "construction": true});
            skLineSegment(sketch, "E115", {"start": v(121.6, -56.4) * mm, "end": v(121.6, -61.6) * mm, "construction": true});
            skCircle(sketch, "E116", {"center": v(121.6, -61.6) * mm, "radius": 3.25 * mm});
            skCircle(sketch, "E117.cCircle", {"center": v(136.6, -61.6) * mm, "radius": 5.2 * mm, "construction": true});
            skLineSegment(sketch, "E117.0", {"start": v(135.05, -55.8) * mm, "end": v(140.85, -57.35) * mm});
            skLineSegment(sketch, "E117.1", {"start": v(140.85, -57.35) * mm, "end": v(142.4, -63.15) * mm});
            skLineSegment(sketch, "E117.2", {"start": v(142.4, -63.15) * mm, "end": v(138.15, -67.4) * mm});
            skLineSegment(sketch, "E117.3", {"start": v(138.15, -67.4) * mm, "end": v(132.35, -65.85) * mm});
            skLineSegment(sketch, "E117.4", {"start": v(132.35, -65.85) * mm, "end": v(130.8, -60.05) * mm});
            skLineSegment(sketch, "E117.5", {"start": v(130.8, -60.05) * mm, "end": v(135.05, -55.8) * mm});
            skPoint(sketch, "E117.0.midPoint", {"position": v(137.95, -56.58) * mm});
            skLineSegment(sketch, "E118", {"start": v(137.95, -56.58) * mm, "end": v(136.6, -61.6) * mm, "construction": true});
            skLineSegment(sketch, "E119", {"start": v(136.6, -56.4) * mm, "end": v(136.6, -61.6) * mm, "construction": true});
            skCircle(sketch, "E120", {"center": v(136.6, -61.6) * mm, "radius": 3.25 * mm});
            skCircle(sketch, "E121.cCircle", {"center": v(151.6, -61.6) * mm, "radius": 5.2 * mm, "construction": true});
            skLineSegment(sketch, "E121.0", {"start": v(150.05, -55.8) * mm, "end": v(155.85, -57.35) * mm});
            skLineSegment(sketch, "E121.1", {"start": v(155.85, -57.35) * mm, "end": v(157.4, -63.15) * mm});
            skLineSegment(sketch, "E121.2", {"start": v(157.4, -63.15) * mm, "end": v(153.15, -67.4) * mm});
            skLineSegment(sketch, "E121.3", {"start": v(153.15, -67.4) * mm, "end": v(147.35, -65.85) * mm});
            skLineSegment(sketch, "E121.4", {"start": v(147.35, -65.85) * mm, "end": v(145.8, -60.05) * mm});
            skLineSegment(sketch, "E121.5", {"start": v(145.8, -60.05) * mm, "end": v(150.05, -55.8) * mm});
            skPoint(sketch, "E121.0.midPoint", {"position": v(152.95, -56.58) * mm});
            skLineSegment(sketch, "E122", {"start": v(152.95, -56.58) * mm, "end": v(151.6, -61.6) * mm, "construction": true});
            skLineSegment(sketch, "E123", {"start": v(151.6, -56.4) * mm, "end": v(151.6, -61.6) * mm, "construction": true});
            skCircle(sketch, "E124", {"center": v(151.6, -61.6) * mm, "radius": 3.25 * mm});
            skCircle(sketch, "E125.cCircle", {"center": v(176.6, -61.6) * mm, "radius": 5.2 * mm, "construction": true});
            skLineSegment(sketch, "E125.0", {"start": v(175.05, -55.8) * mm, "end": v(180.85, -57.35) * mm});
            skLineSegment(sketch, "E125.1", {"start": v(180.85, -57.35) * mm, "end": v(182.4, -63.15) * mm});
            skLineSegment(sketch, "E125.2", {"start": v(182.4, -63.15) * mm, "end": v(178.15, -67.4) * mm});
            skLineSegment(sketch, "E125.3", {"start": v(178.15, -67.4) * mm, "end": v(172.35, -65.85) * mm});
            skLineSegment(sketch, "E125.4", {"start": v(172.35, -65.85) * mm, "end": v(170.8, -60.05) * mm});
            skLineSegment(sketch, "E125.5", {"start": v(170.8, -60.05) * mm, "end": v(175.05, -55.8) * mm});
            skPoint(sketch, "E125.0.midPoint", {"position": v(177.95, -56.58) * mm});
            skLineSegment(sketch, "E126", {"start": v(177.95, -56.58) * mm, "end": v(176.6, -61.6) * mm, "construction": true});
            skLineSegment(sketch, "E127", {"start": v(176.6, -56.4) * mm, "end": v(176.6, -61.6) * mm, "construction": true});
            skCircle(sketch, "E128", {"center": v(176.6, -61.6) * mm, "radius": 3.25 * mm});
            skCircle(sketch, "E129.cCircle", {"center": v(26.6, -76.6) * mm, "radius": 5.2 * mm, "construction": true});
            skLineSegment(sketch, "E129.0", {"start": v(25.05, -70.8) * mm, "end": v(30.85, -72.35) * mm});
            skLineSegment(sketch, "E129.1", {"start": v(30.85, -72.35) * mm, "end": v(32.4, -78.15) * mm});
            skLineSegment(sketch, "E129.2", {"start": v(32.4, -78.15) * mm, "end": v(28.15, -82.4) * mm});
            skLineSegment(sketch, "E129.3", {"start": v(28.15, -82.4) * mm, "end": v(22.35, -80.85) * mm});
            skLineSegment(sketch, "E129.4", {"start": v(22.35, -80.85) * mm, "end": v(20.8, -75.05) * mm});
            skLineSegment(sketch, "E129.5", {"start": v(20.8, -75.05) * mm, "end": v(25.05, -70.8) * mm});
            skPoint(sketch, "E129.0.midPoint", {"position": v(27.95, -71.58) * mm});
            skLineSegment(sketch, "E130", {"start": v(27.95, -71.58) * mm, "end": v(26.6, -76.6) * mm, "construction": true});
            skLineSegment(sketch, "E131", {"start": v(26.6, -71.4) * mm, "end": v(26.6, -76.6) * mm, "construction": true});
            skCircle(sketch, "E132", {"center": v(26.6, -76.6) * mm, "radius": 3.25 * mm});
            skCircle(sketch, "E133.cCircle", {"center": v(46.6, -76.6) * mm, "radius": 5.2 * mm, "construction": true});
            skLineSegment(sketch, "E133.0", {"start": v(45.05, -70.8) * mm, "end": v(50.85, -72.35) * mm});
            skLineSegment(sketch, "E133.1", {"start": v(50.85, -72.35) * mm, "end": v(52.4, -78.15) * mm});
            skLineSegment(sketch, "E133.2", {"start": v(52.4, -78.15) * mm, "end": v(48.15, -82.4) * mm});
            skLineSegment(sketch, "E133.3", {"start": v(48.15, -82.4) * mm, "end": v(42.35, -80.85) * mm});
            skLineSegment(sketch, "E133.4", {"start": v(42.35, -80.85) * mm, "end": v(40.8, -75.05) * mm});
            skLineSegment(sketch, "E133.5", {"start": v(40.8, -75.05) * mm, "end": v(45.05, -70.8) * mm});
            skPoint(sketch, "E133.0.midPoint", {"position": v(47.95, -71.58) * mm});
            skLineSegment(sketch, "E134", {"start": v(47.95, -71.58) * mm, "end": v(46.6, -76.6) * mm, "construction": true});
            skLineSegment(sketch, "E135", {"start": v(46.6, -71.4) * mm, "end": v(46.6, -76.6) * mm, "construction": true});
            skCircle(sketch, "E136", {"center": v(46.6, -76.6) * mm, "radius": 3.25 * mm});
            skCircle(sketch, "E137.cCircle", {"center": v(61.6, -76.6) * mm, "radius": 5.2 * mm, "construction": true});
            skLineSegment(sketch, "E137.0", {"start": v(60.05, -70.8) * mm, "end": v(65.85, -72.35) * mm});
            skLineSegment(sketch, "E137.1", {"start": v(65.85, -72.35) * mm, "end": v(67.4, -78.15) * mm});
            skLineSegment(sketch, "E137.2", {"start": v(67.4, -78.15) * mm, "end": v(63.15, -82.4) * mm});
            skLineSegment(sketch, "E137.3", {"start": v(63.15, -82.4) * mm, "end": v(57.35, -80.85) * mm});
            skLineSegment(sketch, "E137.4", {"start": v(57.35, -80.85) * mm, "end": v(55.8, -75.05) * mm});
            skLineSegment(sketch, "E137.5", {"start": v(55.8, -75.05) * mm, "end": v(60.05, -70.8) * mm});
            skPoint(sketch, "E137.0.midPoint", {"position": v(62.95, -71.58) * mm});
            skLineSegment(sketch, "E138", {"start": v(62.95, -71.58) * mm, "end": v(61.6, -76.6) * mm, "construction": true});
            skLineSegment(sketch, "E139", {"start": v(61.6, -71.4) * mm, "end": v(61.6, -76.6) * mm, "construction": true});
            skCircle(sketch, "E140", {"center": v(61.6, -76.6) * mm, "radius": 3.25 * mm});
            skCircle(sketch, "E141.cCircle", {"center": v(76.6, -76.6) * mm, "radius": 5.2 * mm, "construction": true});
            skLineSegment(sketch, "E141.0", {"start": v(75.05, -70.8) * mm, "end": v(80.85, -72.35) * mm});
            skLineSegment(sketch, "E141.1", {"start": v(80.85, -72.35) * mm, "end": v(82.4, -78.15) * mm});
            skLineSegment(sketch, "E141.2", {"start": v(82.4, -78.15) * mm, "end": v(78.15, -82.4) * mm});
            skLineSegment(sketch, "E141.3", {"start": v(78.15, -82.4) * mm, "end": v(72.35, -80.85) * mm});
            skLineSegment(sketch, "E141.4", {"start": v(72.35, -80.85) * mm, "end": v(70.8, -75.05) * mm});
            skLineSegment(sketch, "E141.5", {"start": v(70.8, -75.05) * mm, "end": v(75.05, -70.8) * mm});
            skPoint(sketch, "E141.0.midPoint", {"position": v(77.95, -71.58) * mm});
            skLineSegment(sketch, "E142", {"start": v(77.95, -71.58) * mm, "end": v(76.6, -76.6) * mm, "construction": true});
            skLineSegment(sketch, "E143", {"start": v(76.6, -71.4) * mm, "end": v(76.6, -76.6) * mm, "construction": true});
            skCircle(sketch, "E144", {"center": v(76.6, -76.6) * mm, "radius": 3.25 * mm});
            skCircle(sketch, "E145.cCircle", {"center": v(91.6, -76.6) * mm, "radius": 5.2 * mm, "construction": true});
            skLineSegment(sketch, "E145.0", {"start": v(90.05, -70.8) * mm, "end": v(95.85, -72.35) * mm});
            skLineSegment(sketch, "E145.1", {"start": v(95.85, -72.35) * mm, "end": v(97.4, -78.15) * mm});
            skLineSegment(sketch, "E145.2", {"start": v(97.4, -78.15) * mm, "end": v(93.15, -82.4) * mm});
            skLineSegment(sketch, "E145.3", {"start": v(93.15, -82.4) * mm, "end": v(87.35, -80.85) * mm});
            skLineSegment(sketch, "E145.4", {"start": v(87.35, -80.85) * mm, "end": v(85.8, -75.05) * mm});
            skLineSegment(sketch, "E145.5", {"start": v(85.8, -75.05) * mm, "end": v(90.05, -70.8) * mm});
            skPoint(sketch, "E145.0.midPoint", {"position": v(92.95, -71.58) * mm});
            skLineSegment(sketch, "E146", {"start": v(92.95, -71.58) * mm, "end": v(91.6, -76.6) * mm, "construction": true});
            skLineSegment(sketch, "E147", {"start": v(91.6, -71.4) * mm, "end": v(91.6, -76.6) * mm, "construction": true});
            skCircle(sketch, "E148", {"center": v(91.6, -76.6) * mm, "radius": 3.25 * mm});
            skCircle(sketch, "E149.cCircle", {"center": v(106.6, -76.6) * mm, "radius": 5.2 * mm, "construction": true});
            skLineSegment(sketch, "E149.0", {"start": v(105.05, -70.8) * mm, "end": v(110.85, -72.35) * mm});
            skLineSegment(sketch, "E149.1", {"start": v(110.85, -72.35) * mm, "end": v(112.4, -78.15) * mm});
            skLineSegment(sketch, "E149.2", {"start": v(112.4, -78.15) * mm, "end": v(108.15, -82.4) * mm});
            skLineSegment(sketch, "E149.3", {"start": v(108.15, -82.4) * mm, "end": v(102.35, -80.85) * mm});
            skLineSegment(sketch, "E149.4", {"start": v(102.35, -80.85) * mm, "end": v(100.8, -75.05) * mm});
            skLineSegment(sketch, "E149.5", {"start": v(100.8, -75.05) * mm, "end": v(105.05, -70.8) * mm});
            skPoint(sketch, "E149.0.midPoint", {"position": v(107.95, -71.58) * mm});
            skLineSegment(sketch, "E150", {"start": v(107.95, -71.58) * mm, "end": v(106.6, -76.6) * mm, "construction": true});
            skLineSegment(sketch, "E151", {"start": v(106.6, -71.4) * mm, "end": v(106.6, -76.6) * mm, "construction": true});
            skCircle(sketch, "E152", {"center": v(106.6, -76.6) * mm, "radius": 3.25 * mm});
            skCircle(sketch, "E153.cCircle", {"center": v(121.6, -76.6) * mm, "radius": 5.2 * mm, "construction": true});
            skLineSegment(sketch, "E153.0", {"start": v(120.05, -70.8) * mm, "end": v(125.85, -72.35) * mm});
            skLineSegment(sketch, "E153.1", {"start": v(125.85, -72.35) * mm, "end": v(127.4, -78.15) * mm});
            skLineSegment(sketch, "E153.2", {"start": v(127.4, -78.15) * mm, "end": v(123.15, -82.4) * mm});
            skLineSegment(sketch, "E153.3", {"start": v(123.15, -82.4) * mm, "end": v(117.35, -80.85) * mm});
            skLineSegment(sketch, "E153.4", {"start": v(117.35, -80.85) * mm, "end": v(115.8, -75.05) * mm});
            skLineSegment(sketch, "E153.5", {"start": v(115.8, -75.05) * mm, "end": v(120.05, -70.8) * mm});
            skPoint(sketch, "E153.0.midPoint", {"position": v(122.95, -71.58) * mm});
            skLineSegment(sketch, "E154", {"start": v(122.95, -71.58) * mm, "end": v(121.6, -76.6) * mm, "construction": true});
            skLineSegment(sketch, "E155", {"start": v(121.6, -71.4) * mm, "end": v(121.6, -76.6) * mm, "construction": true});
            skCircle(sketch, "E156", {"center": v(121.6, -76.6) * mm, "radius": 3.25 * mm});
            skCircle(sketch, "E157.cCircle", {"center": v(136.6, -76.6) * mm, "radius": 5.2 * mm, "construction": true});
            skLineSegment(sketch, "E157.0", {"start": v(135.05, -70.8) * mm, "end": v(140.85, -72.35) * mm});
            skLineSegment(sketch, "E157.1", {"start": v(140.85, -72.35) * mm, "end": v(142.4, -78.15) * mm});
            skLineSegment(sketch, "E157.2", {"start": v(142.4, -78.15) * mm, "end": v(138.15, -82.4) * mm});
            skLineSegment(sketch, "E157.3", {"start": v(138.15, -82.4) * mm, "end": v(132.35, -80.85) * mm});
            skLineSegment(sketch, "E157.4", {"start": v(132.35, -80.85) * mm, "end": v(130.8, -75.05) * mm});
            skLineSegment(sketch, "E157.5", {"start": v(130.8, -75.05) * mm, "end": v(135.05, -70.8) * mm});
            skPoint(sketch, "E157.0.midPoint", {"position": v(137.95, -71.58) * mm});
            skLineSegment(sketch, "E158", {"start": v(137.95, -71.58) * mm, "end": v(136.6, -76.6) * mm, "construction": true});
            skLineSegment(sketch, "E159", {"start": v(136.6, -71.4) * mm, "end": v(136.6, -76.6) * mm, "construction": true});
            skCircle(sketch, "E160", {"center": v(136.6, -76.6) * mm, "radius": 3.25 * mm});
            skCircle(sketch, "E161.cCircle", {"center": v(151.6, -76.6) * mm, "radius": 5.2 * mm, "construction": true});
            skLineSegment(sketch, "E161.0", {"start": v(150.05, -70.8) * mm, "end": v(155.85, -72.35) * mm});
            skLineSegment(sketch, "E161.1", {"start": v(155.85, -72.35) * mm, "end": v(157.4, -78.15) * mm});
            skLineSegment(sketch, "E161.2", {"start": v(157.4, -78.15) * mm, "end": v(153.15, -82.4) * mm});
            skLineSegment(sketch, "E161.3", {"start": v(153.15, -82.4) * mm, "end": v(147.35, -80.85) * mm});
            skLineSegment(sketch, "E161.4", {"start": v(147.35, -80.85) * mm, "end": v(145.8, -75.05) * mm});
            skLineSegment(sketch, "E161.5", {"start": v(145.8, -75.05) * mm, "end": v(150.05, -70.8) * mm});
            skPoint(sketch, "E161.0.midPoint", {"position": v(152.95, -71.58) * mm});
            skLineSegment(sketch, "E162", {"start": v(152.95, -71.58) * mm, "end": v(151.6, -76.6) * mm, "construction": true});
            skLineSegment(sketch, "E163", {"start": v(151.6, -71.4) * mm, "end": v(151.6, -76.6) * mm, "construction": true});
            skCircle(sketch, "E164", {"center": v(151.6, -76.6) * mm, "radius": 3.25 * mm});
            skCircle(sketch, "E165.cCircle", {"center": v(176.6, -76.6) * mm, "radius": 5.2 * mm, "construction": true});
            skLineSegment(sketch, "E165.0", {"start": v(175.05, -70.8) * mm, "end": v(180.85, -72.35) * mm});
            skLineSegment(sketch, "E165.1", {"start": v(180.85, -72.35) * mm, "end": v(182.4, -78.15) * mm});
            skLineSegment(sketch, "E165.2", {"start": v(182.4, -78.15) * mm, "end": v(178.15, -82.4) * mm});
            skLineSegment(sketch, "E165.3", {"start": v(178.15, -82.4) * mm, "end": v(172.35, -80.85) * mm});
            skLineSegment(sketch, "E165.4", {"start": v(172.35, -80.85) * mm, "end": v(170.8, -75.05) * mm});
            skLineSegment(sketch, "E165.5", {"start": v(170.8, -75.05) * mm, "end": v(175.05, -70.8) * mm});
            skPoint(sketch, "E165.0.midPoint", {"position": v(177.95, -71.58) * mm});
            skLineSegment(sketch, "E166", {"start": v(177.95, -71.58) * mm, "end": v(176.6, -76.6) * mm, "construction": true});
            skLineSegment(sketch, "E167", {"start": v(176.6, -71.4) * mm, "end": v(176.6, -76.6) * mm, "construction": true});
            skCircle(sketch, "E168", {"center": v(176.6, -76.6) * mm, "radius": 3.25 * mm});
            skCircle(sketch, "E169.cCircle", {"center": v(26.6, -91.6) * mm, "radius": 5.2 * mm, "construction": true});
            skLineSegment(sketch, "E169.0", {"start": v(25.05, -85.8) * mm, "end": v(30.85, -87.35) * mm});
            skLineSegment(sketch, "E169.1", {"start": v(30.85, -87.35) * mm, "end": v(32.4, -93.15) * mm});
            skLineSegment(sketch, "E169.2", {"start": v(32.4, -93.15) * mm, "end": v(28.15, -97.4) * mm});
            skLineSegment(sketch, "E169.3", {"start": v(28.15, -97.4) * mm, "end": v(22.35, -95.85) * mm});
            skLineSegment(sketch, "E169.4", {"start": v(22.35, -95.85) * mm, "end": v(20.8, -90.05) * mm});
            skLineSegment(sketch, "E169.5", {"start": v(20.8, -90.05) * mm, "end": v(25.05, -85.8) * mm});
            skPoint(sketch, "E169.0.midPoint", {"position": v(27.95, -86.58) * mm});
            skLineSegment(sketch, "E170", {"start": v(27.95, -86.58) * mm, "end": v(26.6, -91.6) * mm, "construction": true});
            skLineSegment(sketch, "E171", {"start": v(26.6, -86.4) * mm, "end": v(26.6, -91.6) * mm, "construction": true});
            skCircle(sketch, "E172", {"center": v(26.6, -91.6) * mm, "radius": 3.25 * mm});
            skCircle(sketch, "E173.cCircle", {"center": v(46.6, -91.6) * mm, "radius": 5.2 * mm, "construction": true});
            skLineSegment(sketch, "E173.0", {"start": v(45.05, -85.8) * mm, "end": v(50.85, -87.35) * mm});
            skLineSegment(sketch, "E173.1", {"start": v(50.85, -87.35) * mm, "end": v(52.4, -93.15) * mm});
            skLineSegment(sketch, "E173.2", {"start": v(52.4, -93.15) * mm, "end": v(48.15, -97.4) * mm});
            skLineSegment(sketch, "E173.3", {"start": v(48.15, -97.4) * mm, "end": v(42.35, -95.85) * mm});
            skLineSegment(sketch, "E173.4", {"start": v(42.35, -95.85) * mm, "end": v(40.8, -90.05) * mm});
            skLineSegment(sketch, "E173.5", {"start": v(40.8, -90.05) * mm, "end": v(45.05, -85.8) * mm});
            skPoint(sketch, "E173.0.midPoint", {"position": v(47.95, -86.58) * mm});
            skLineSegment(sketch, "E174", {"start": v(47.95, -86.58) * mm, "end": v(46.6, -91.6) * mm, "construction": true});
            skLineSegment(sketch, "E175", {"start": v(46.6, -86.4) * mm, "end": v(46.6, -91.6) * mm, "construction": true});
            skCircle(sketch, "E176", {"center": v(46.6, -91.6) * mm, "radius": 3.25 * mm});
            skCircle(sketch, "E177.cCircle", {"center": v(61.6, -91.6) * mm, "radius": 5.2 * mm, "construction": true});
            skLineSegment(sketch, "E177.0", {"start": v(60.05, -85.8) * mm, "end": v(65.85, -87.35) * mm});
            skLineSegment(sketch, "E177.1", {"start": v(65.85, -87.35) * mm, "end": v(67.4, -93.15) * mm});
            skLineSegment(sketch, "E177.2", {"start": v(67.4, -93.15) * mm, "end": v(63.15, -97.4) * mm});
            skLineSegment(sketch, "E177.3", {"start": v(63.15, -97.4) * mm, "end": v(57.35, -95.85) * mm});
            skLineSegment(sketch, "E177.4", {"start": v(57.35, -95.85) * mm, "end": v(55.8, -90.05) * mm});
            skLineSegment(sketch, "E177.5", {"start": v(55.8, -90.05) * mm, "end": v(60.05, -85.8) * mm});
            skPoint(sketch, "E177.0.midPoint", {"position": v(62.95, -86.58) * mm});
            skLineSegment(sketch, "E178", {"start": v(62.95, -86.58) * mm, "end": v(61.6, -91.6) * mm, "construction": true});
            skLineSegment(sketch, "E179", {"start": v(61.6, -86.4) * mm, "end": v(61.6, -91.6) * mm, "construction": true});
            skCircle(sketch, "E180", {"center": v(61.6, -91.6) * mm, "radius": 3.25 * mm});
            skCircle(sketch, "E181.cCircle", {"center": v(76.6, -91.6) * mm, "radius": 5.2 * mm, "construction": true});
            skLineSegment(sketch, "E181.0", {"start": v(75.05, -85.8) * mm, "end": v(80.85, -87.35) * mm});
            skLineSegment(sketch, "E181.1", {"start": v(80.85, -87.35) * mm, "end": v(82.4, -93.15) * mm});
            skLineSegment(sketch, "E181.2", {"start": v(82.4, -93.15) * mm, "end": v(78.15, -97.4) * mm});
            skLineSegment(sketch, "E181.3", {"start": v(78.15, -97.4) * mm, "end": v(72.35, -95.85) * mm});
            skLineSegment(sketch, "E181.4", {"start": v(72.35, -95.85) * mm, "end": v(70.8, -90.05) * mm});
            skLineSegment(sketch, "E181.5", {"start": v(70.8, -90.05) * mm, "end": v(75.05, -85.8) * mm});
            skPoint(sketch, "E181.0.midPoint", {"position": v(77.95, -86.58) * mm});
            skLineSegment(sketch, "E182", {"start": v(77.95, -86.58) * mm, "end": v(76.6, -91.6) * mm, "construction": true});
            skLineSegment(sketch, "E183", {"start": v(76.6, -86.4) * mm, "end": v(76.6, -91.6) * mm, "construction": true});
            skCircle(sketch, "E184", {"center": v(76.6, -91.6) * mm, "radius": 3.25 * mm});
            skCircle(sketch, "E185.cCircle", {"center": v(91.6, -91.6) * mm, "radius": 5.2 * mm, "construction": true});
            skLineSegment(sketch, "E185.0", {"start": v(90.05, -85.8) * mm, "end": v(95.85, -87.35) * mm});
            skLineSegment(sketch, "E185.1", {"start": v(95.85, -87.35) * mm, "end": v(97.4, -93.15) * mm});
            skLineSegment(sketch, "E185.2", {"start": v(97.4, -93.15) * mm, "end": v(93.15, -97.4) * mm});
            skLineSegment(sketch, "E185.3", {"start": v(93.15, -97.4) * mm, "end": v(87.35, -95.85) * mm});
            skLineSegment(sketch, "E185.4", {"start": v(87.35, -95.85) * mm, "end": v(85.8, -90.05) * mm});
            skLineSegment(sketch, "E185.5", {"start": v(85.8, -90.05) * mm, "end": v(90.05, -85.8) * mm});
            skPoint(sketch, "E185.0.midPoint", {"position": v(92.95, -86.58) * mm});
            skLineSegment(sketch, "E186", {"start": v(92.95, -86.58) * mm, "end": v(91.6, -91.6) * mm, "construction": true});
            skLineSegment(sketch, "E187", {"start": v(91.6, -86.4) * mm, "end": v(91.6, -91.6) * mm, "construction": true});
            skCircle(sketch, "E188", {"center": v(91.6, -91.6) * mm, "radius": 3.25 * mm});
            skCircle(sketch, "E189.cCircle", {"center": v(106.6, -91.6) * mm, "radius": 5.2 * mm, "construction": true});
            skLineSegment(sketch, "E189.0", {"start": v(105.05, -85.8) * mm, "end": v(110.85, -87.35) * mm});
            skLineSegment(sketch, "E189.1", {"start": v(110.85, -87.35) * mm, "end": v(112.4, -93.15) * mm});
            skLineSegment(sketch, "E189.2", {"start": v(112.4, -93.15) * mm, "end": v(108.15, -97.4) * mm});
            skLineSegment(sketch, "E189.3", {"start": v(108.15, -97.4) * mm, "end": v(102.35, -95.85) * mm});
            skLineSegment(sketch, "E189.4", {"start": v(102.35, -95.85) * mm, "end": v(100.8, -90.05) * mm});
            skLineSegment(sketch, "E189.5", {"start": v(100.8, -90.05) * mm, "end": v(105.05, -85.8) * mm});
            skPoint(sketch, "E189.0.midPoint", {"position": v(107.95, -86.58) * mm});
            skLineSegment(sketch, "E190", {"start": v(107.95, -86.58) * mm, "end": v(106.6, -91.6) * mm, "construction": true});
            skLineSegment(sketch, "E191", {"start": v(106.6, -86.4) * mm, "end": v(106.6, -91.6) * mm, "construction": true});
            skCircle(sketch, "E192", {"center": v(106.6, -91.6) * mm, "radius": 3.25 * mm});
            skCircle(sketch, "E193.cCircle", {"center": v(121.6, -91.6) * mm, "radius": 5.2 * mm, "construction": true});
            skLineSegment(sketch, "E193.0", {"start": v(120.05, -85.8) * mm, "end": v(125.85, -87.35) * mm});
            skLineSegment(sketch, "E193.1", {"start": v(125.85, -87.35) * mm, "end": v(127.4, -93.15) * mm});
            skLineSegment(sketch, "E193.2", {"start": v(127.4, -93.15) * mm, "end": v(123.15, -97.4) * mm});
            skLineSegment(sketch, "E193.3", {"start": v(123.15, -97.4) * mm, "end": v(117.35, -95.85) * mm});
            skLineSegment(sketch, "E193.4", {"start": v(117.35, -95.85) * mm, "end": v(115.8, -90.05) * mm});
            skLineSegment(sketch, "E193.5", {"start": v(115.8, -90.05) * mm, "end": v(120.05, -85.8) * mm});
            skPoint(sketch, "E193.0.midPoint", {"position": v(122.95, -86.58) * mm});
            skLineSegment(sketch, "E194", {"start": v(122.95, -86.58) * mm, "end": v(121.6, -91.6) * mm, "construction": true});
            skLineSegment(sketch, "E195", {"start": v(121.6, -86.4) * mm, "end": v(121.6, -91.6) * mm, "construction": true});
            skCircle(sketch, "E196", {"center": v(121.6, -91.6) * mm, "radius": 3.25 * mm});
            skCircle(sketch, "E197.cCircle", {"center": v(136.6, -91.6) * mm, "radius": 5.2 * mm, "construction": true});
            skLineSegment(sketch, "E197.0", {"start": v(135.05, -85.8) * mm, "end": v(140.85, -87.35) * mm});
            skLineSegment(sketch, "E197.1", {"start": v(140.85, -87.35) * mm, "end": v(142.4, -93.15) * mm});
            skLineSegment(sketch, "E197.2", {"start": v(142.4, -93.15) * mm, "end": v(138.15, -97.4) * mm});
            skLineSegment(sketch, "E197.3", {"start": v(138.15, -97.4) * mm, "end": v(132.35, -95.85) * mm});
            skLineSegment(sketch, "E197.4", {"start": v(132.35, -95.85) * mm, "end": v(130.8, -90.05) * mm});
            skLineSegment(sketch, "E197.5", {"start": v(130.8, -90.05) * mm, "end": v(135.05, -85.8) * mm});
            skPoint(sketch, "E197.0.midPoint", {"position": v(137.95, -86.58) * mm});
            skLineSegment(sketch, "E198", {"start": v(137.95, -86.58) * mm, "end": v(136.6, -91.6) * mm, "construction": true});
            skLineSegment(sketch, "E199", {"start": v(136.6, -86.4) * mm, "end": v(136.6, -91.6) * mm, "construction": true});
            skCircle(sketch, "E200", {"center": v(136.6, -91.6) * mm, "radius": 3.25 * mm});
            skCircle(sketch, "E201.cCircle", {"center": v(151.6, -91.6) * mm, "radius": 5.2 * mm, "construction": true});
            skLineSegment(sketch, "E201.0", {"start": v(150.05, -85.8) * mm, "end": v(155.85, -87.35) * mm});
            skLineSegment(sketch, "E201.1", {"start": v(155.85, -87.35) * mm, "end": v(157.4, -93.15) * mm});
            skLineSegment(sketch, "E201.2", {"start": v(157.4, -93.15) * mm, "end": v(153.15, -97.4) * mm});
            skLineSegment(sketch, "E201.3", {"start": v(153.15, -97.4) * mm, "end": v(147.35, -95.85) * mm});
            skLineSegment(sketch, "E201.4", {"start": v(147.35, -95.85) * mm, "end": v(145.8, -90.05) * mm});
            skLineSegment(sketch, "E201.5", {"start": v(145.8, -90.05) * mm, "end": v(150.05, -85.8) * mm});
            skPoint(sketch, "E201.0.midPoint", {"position": v(152.95, -86.58) * mm});
            skLineSegment(sketch, "E202", {"start": v(152.95, -86.58) * mm, "end": v(151.6, -91.6) * mm, "construction": true});
            skLineSegment(sketch, "E203", {"start": v(151.6, -86.4) * mm, "end": v(151.6, -91.6) * mm, "construction": true});
            skCircle(sketch, "E204", {"center": v(151.6, -91.6) * mm, "radius": 3.25 * mm});
            skCircle(sketch, "E205.cCircle", {"center": v(176.6, -91.6) * mm, "radius": 5.2 * mm, "construction": true});
            skLineSegment(sketch, "E205.0", {"start": v(175.05, -85.8) * mm, "end": v(180.85, -87.35) * mm});
            skLineSegment(sketch, "E205.1", {"start": v(180.85, -87.35) * mm, "end": v(182.4, -93.15) * mm});
            skLineSegment(sketch, "E205.2", {"start": v(182.4, -93.15) * mm, "end": v(178.15, -97.4) * mm});
            skLineSegment(sketch, "E205.3", {"start": v(178.15, -97.4) * mm, "end": v(172.35, -95.85) * mm});
            skLineSegment(sketch, "E205.4", {"start": v(172.35, -95.85) * mm, "end": v(170.8, -90.05) * mm});
            skLineSegment(sketch, "E205.5", {"start": v(170.8, -90.05) * mm, "end": v(175.05, -85.8) * mm});
            skPoint(sketch, "E205.0.midPoint", {"position": v(177.95, -86.58) * mm});
            skLineSegment(sketch, "E206", {"start": v(177.95, -86.58) * mm, "end": v(176.6, -91.6) * mm, "construction": true});
            skLineSegment(sketch, "E207", {"start": v(176.6, -86.4) * mm, "end": v(176.6, -91.6) * mm, "construction": true});
            skCircle(sketch, "E208", {"center": v(176.6, -91.6) * mm, "radius": 3.25 * mm});
            skCircle(sketch, "E209.cCircle", {"center": v(26.6, -106.6) * mm, "radius": 5.2 * mm, "construction": true});
            skLineSegment(sketch, "E209.0", {"start": v(25.05, -100.8) * mm, "end": v(30.85, -102.35) * mm});
            skLineSegment(sketch, "E209.1", {"start": v(30.85, -102.35) * mm, "end": v(32.4, -108.15) * mm});
            skLineSegment(sketch, "E209.2", {"start": v(32.4, -108.15) * mm, "end": v(28.15, -112.4) * mm});
            skLineSegment(sketch, "E209.3", {"start": v(28.15, -112.4) * mm, "end": v(22.35, -110.85) * mm});
            skLineSegment(sketch, "E209.4", {"start": v(22.35, -110.85) * mm, "end": v(20.8, -105.05) * mm});
            skLineSegment(sketch, "E209.5", {"start": v(20.8, -105.05) * mm, "end": v(25.05, -100.8) * mm});
            skPoint(sketch, "E209.0.midPoint", {"position": v(27.95, -101.58) * mm});
            skLineSegment(sketch, "E210", {"start": v(27.95, -101.58) * mm, "end": v(26.6, -106.6) * mm, "construction": true});
            skLineSegment(sketch, "E211", {"start": v(26.6, -101.4) * mm, "end": v(26.6, -106.6) * mm, "construction": true});
            skCircle(sketch, "E212", {"center": v(26.6, -106.6) * mm, "radius": 3.25 * mm});
            skCircle(sketch, "E213.cCircle", {"center": v(46.6, -106.6) * mm, "radius": 5.2 * mm, "construction": true});
            skLineSegment(sketch, "E213.0", {"start": v(45.05, -100.8) * mm, "end": v(50.85, -102.35) * mm});
            skLineSegment(sketch, "E213.1", {"start": v(50.85, -102.35) * mm, "end": v(52.4, -108.15) * mm});
            skLineSegment(sketch, "E213.2", {"start": v(52.4, -108.15) * mm, "end": v(48.15, -112.4) * mm});
            skLineSegment(sketch, "E213.3", {"start": v(48.15, -112.4) * mm, "end": v(42.35, -110.85) * mm});
            skLineSegment(sketch, "E213.4", {"start": v(42.35, -110.85) * mm, "end": v(40.8, -105.05) * mm});
            skLineSegment(sketch, "E213.5", {"start": v(40.8, -105.05) * mm, "end": v(45.05, -100.8) * mm});
            skPoint(sketch, "E213.0.midPoint", {"position": v(47.95, -101.58) * mm});
            skLineSegment(sketch, "E214", {"start": v(47.95, -101.58) * mm, "end": v(46.6, -106.6) * mm, "construction": true});
            skLineSegment(sketch, "E215", {"start": v(46.6, -101.4) * mm, "end": v(46.6, -106.6) * mm, "construction": true});
            skCircle(sketch, "E216", {"center": v(46.6, -106.6) * mm, "radius": 3.25 * mm});
            skCircle(sketch, "E217.cCircle", {"center": v(61.6, -106.6) * mm, "radius": 5.2 * mm, "construction": true});
            skLineSegment(sketch, "E217.0", {"start": v(60.05, -100.8) * mm, "end": v(65.85, -102.35) * mm});
            skLineSegment(sketch, "E217.1", {"start": v(65.85, -102.35) * mm, "end": v(67.4, -108.15) * mm});
            skLineSegment(sketch, "E217.2", {"start": v(67.4, -108.15) * mm, "end": v(63.15, -112.4) * mm});
            skLineSegment(sketch, "E217.3", {"start": v(63.15, -112.4) * mm, "end": v(57.35, -110.85) * mm});
            skLineSegment(sketch, "E217.4", {"start": v(57.35, -110.85) * mm, "end": v(55.8, -105.05) * mm});
            skLineSegment(sketch, "E217.5", {"start": v(55.8, -105.05) * mm, "end": v(60.05, -100.8) * mm});
            skPoint(sketch, "E217.0.midPoint", {"position": v(62.95, -101.58) * mm});
            skLineSegment(sketch, "E218", {"start": v(62.95, -101.58) * mm, "end": v(61.6, -106.6) * mm, "construction": true});
            skLineSegment(sketch, "E219", {"start": v(61.6, -101.4) * mm, "end": v(61.6, -106.6) * mm, "construction": true});
            skCircle(sketch, "E220", {"center": v(61.6, -106.6) * mm, "radius": 3.25 * mm});
            skCircle(sketch, "E221.cCircle", {"center": v(76.6, -106.6) * mm, "radius": 5.2 * mm, "construction": true});
            skLineSegment(sketch, "E221.0", {"start": v(75.05, -100.8) * mm, "end": v(80.85, -102.35) * mm});
            skLineSegment(sketch, "E221.1", {"start": v(80.85, -102.35) * mm, "end": v(82.4, -108.15) * mm});
            skLineSegment(sketch, "E221.2", {"start": v(82.4, -108.15) * mm, "end": v(78.15, -112.4) * mm});
            skLineSegment(sketch, "E221.3", {"start": v(78.15, -112.4) * mm, "end": v(72.35, -110.85) * mm});
            skLineSegment(sketch, "E221.4", {"start": v(72.35, -110.85) * mm, "end": v(70.8, -105.05) * mm});
            skLineSegment(sketch, "E221.5", {"start": v(70.8, -105.05) * mm, "end": v(75.05, -100.8) * mm});
            skPoint(sketch, "E221.0.midPoint", {"position": v(77.95, -101.58) * mm});
            skLineSegment(sketch, "E222", {"start": v(77.95, -101.58) * mm, "end": v(76.6, -106.6) * mm, "construction": true});
            skLineSegment(sketch, "E223", {"start": v(76.6, -101.4) * mm, "end": v(76.6, -106.6) * mm, "construction": true});
            skCircle(sketch, "E224", {"center": v(76.6, -106.6) * mm, "radius": 3.25 * mm});
            skCircle(sketch, "E225.cCircle", {"center": v(91.6, -106.6) * mm, "radius": 5.2 * mm, "construction": true});
            skLineSegment(sketch, "E225.0", {"start": v(90.05, -100.8) * mm, "end": v(95.85, -102.35) * mm});
            skLineSegment(sketch, "E225.1", {"start": v(95.85, -102.35) * mm, "end": v(97.4, -108.15) * mm});
            skLineSegment(sketch, "E225.2", {"start": v(97.4, -108.15) * mm, "end": v(93.15, -112.4) * mm});
            skLineSegment(sketch, "E225.3", {"start": v(93.15, -112.4) * mm, "end": v(87.35, -110.85) * mm});
            skLineSegment(sketch, "E225.4", {"start": v(87.35, -110.85) * mm, "end": v(85.8, -105.05) * mm});
            skLineSegment(sketch, "E225.5", {"start": v(85.8, -105.05) * mm, "end": v(90.05, -100.8) * mm});
            skPoint(sketch, "E225.0.midPoint", {"position": v(92.95, -101.58) * mm});
            skLineSegment(sketch, "E226", {"start": v(92.95, -101.58) * mm, "end": v(91.6, -106.6) * mm, "construction": true});
            skLineSegment(sketch, "E227", {"start": v(91.6, -101.4) * mm, "end": v(91.6, -106.6) * mm, "construction": true});
            skCircle(sketch, "E228", {"center": v(91.6, -106.6) * mm, "radius": 3.25 * mm});
            skCircle(sketch, "E229.cCircle", {"center": v(106.6, -106.6) * mm, "radius": 5.2 * mm, "construction": true});
            skLineSegment(sketch, "E229.0", {"start": v(105.05, -100.8) * mm, "end": v(110.85, -102.35) * mm});
            skLineSegment(sketch, "E229.1", {"start": v(110.85, -102.35) * mm, "end": v(112.4, -108.15) * mm});
            skLineSegment(sketch, "E229.2", {"start": v(112.4, -108.15) * mm, "end": v(108.15, -112.4) * mm});
            skLineSegment(sketch, "E229.3", {"start": v(108.15, -112.4) * mm, "end": v(102.35, -110.85) * mm});
            skLineSegment(sketch, "E229.4", {"start": v(102.35, -110.85) * mm, "end": v(100.8, -105.05) * mm});
            skLineSegment(sketch, "E229.5", {"start": v(100.8, -105.05) * mm, "end": v(105.05, -100.8) * mm});
            skPoint(sketch, "E229.0.midPoint", {"position": v(107.95, -101.58) * mm});
            skLineSegment(sketch, "E230", {"start": v(107.95, -101.58) * mm, "end": v(106.6, -106.6) * mm, "construction": true});
            skLineSegment(sketch, "E231", {"start": v(106.6, -101.4) * mm, "end": v(106.6, -106.6) * mm, "construction": true});
            skCircle(sketch, "E232", {"center": v(106.6, -106.6) * mm, "radius": 3.25 * mm});
            skCircle(sketch, "E233.cCircle", {"center": v(121.6, -106.6) * mm, "radius": 5.2 * mm, "construction": true});
            skLineSegment(sketch, "E233.0", {"start": v(120.05, -100.8) * mm, "end": v(125.85, -102.35) * mm});
            skLineSegment(sketch, "E233.1", {"start": v(125.85, -102.35) * mm, "end": v(127.4, -108.15) * mm});
            skLineSegment(sketch, "E233.2", {"start": v(127.4, -108.15) * mm, "end": v(123.15, -112.4) * mm});
            skLineSegment(sketch, "E233.3", {"start": v(123.15, -112.4) * mm, "end": v(117.35, -110.85) * mm});
            skLineSegment(sketch, "E233.4", {"start": v(117.35, -110.85) * mm, "end": v(115.8, -105.05) * mm});
            skLineSegment(sketch, "E233.5", {"start": v(115.8, -105.05) * mm, "end": v(120.05, -100.8) * mm});
            skPoint(sketch, "E233.0.midPoint", {"position": v(122.95, -101.58) * mm});
            skLineSegment(sketch, "E234", {"start": v(122.95, -101.58) * mm, "end": v(121.6, -106.6) * mm, "construction": true});
            skLineSegment(sketch, "E235", {"start": v(121.6, -101.4) * mm, "end": v(121.6, -106.6) * mm, "construction": true});
            skCircle(sketch, "E236", {"center": v(121.6, -106.6) * mm, "radius": 3.25 * mm});
            skCircle(sketch, "E237.cCircle", {"center": v(136.6, -106.6) * mm, "radius": 5.2 * mm, "construction": true});
            skLineSegment(sketch, "E237.0", {"start": v(135.05, -100.8) * mm, "end": v(140.85, -102.35) * mm});
            skLineSegment(sketch, "E237.1", {"start": v(140.85, -102.35) * mm, "end": v(142.4, -108.15) * mm});
            skLineSegment(sketch, "E237.2", {"start": v(142.4, -108.15) * mm, "end": v(138.15, -112.4) * mm});
            skLineSegment(sketch, "E237.3", {"start": v(138.15, -112.4) * mm, "end": v(132.35, -110.85) * mm});
            skLineSegment(sketch, "E237.4", {"start": v(132.35, -110.85) * mm, "end": v(130.8, -105.05) * mm});
            skLineSegment(sketch, "E237.5", {"start": v(130.8, -105.05) * mm, "end": v(135.05, -100.8) * mm});
            skPoint(sketch, "E237.0.midPoint", {"position": v(137.95, -101.58) * mm});
            skLineSegment(sketch, "E238", {"start": v(137.95, -101.58) * mm, "end": v(136.6, -106.6) * mm, "construction": true});
            skLineSegment(sketch, "E239", {"start": v(136.6, -101.4) * mm, "end": v(136.6, -106.6) * mm, "construction": true});
            skCircle(sketch, "E240", {"center": v(136.6, -106.6) * mm, "radius": 3.25 * mm});
            skCircle(sketch, "E241.cCircle", {"center": v(151.6, -106.6) * mm, "radius": 5.2 * mm, "construction": true});
            skLineSegment(sketch, "E241.0", {"start": v(150.05, -100.8) * mm, "end": v(155.85, -102.35) * mm});
            skLineSegment(sketch, "E241.1", {"start": v(155.85, -102.35) * mm, "end": v(157.4, -108.15) * mm});
            skLineSegment(sketch, "E241.2", {"start": v(157.4, -108.15) * mm, "end": v(153.15, -112.4) * mm});
            skLineSegment(sketch, "E241.3", {"start": v(153.15, -112.4) * mm, "end": v(147.35, -110.85) * mm});
            skLineSegment(sketch, "E241.4", {"start": v(147.35, -110.85) * mm, "end": v(145.8, -105.05) * mm});
            skLineSegment(sketch, "E241.5", {"start": v(145.8, -105.05) * mm, "end": v(150.05, -100.8) * mm});
            skPoint(sketch, "E241.0.midPoint", {"position": v(152.95, -101.58) * mm});
            skLineSegment(sketch, "E242", {"start": v(152.95, -101.58) * mm, "end": v(151.6, -106.6) * mm, "construction": true});
            skLineSegment(sketch, "E243", {"start": v(151.6, -101.4) * mm, "end": v(151.6, -106.6) * mm, "construction": true});
            skCircle(sketch, "E244", {"center": v(151.6, -106.6) * mm, "radius": 3.25 * mm});
            skCircle(sketch, "E245.cCircle", {"center": v(176.6, -106.6) * mm, "radius": 5.2 * mm, "construction": true});
            skLineSegment(sketch, "E245.0", {"start": v(175.05, -100.8) * mm, "end": v(180.85, -102.35) * mm});
            skLineSegment(sketch, "E245.1", {"start": v(180.85, -102.35) * mm, "end": v(182.4, -108.15) * mm});
            skLineSegment(sketch, "E245.2", {"start": v(182.4, -108.15) * mm, "end": v(178.15, -112.4) * mm});
            skLineSegment(sketch, "E245.3", {"start": v(178.15, -112.4) * mm, "end": v(172.35, -110.85) * mm});
            skLineSegment(sketch, "E245.4", {"start": v(172.35, -110.85) * mm, "end": v(170.8, -105.05) * mm});
            skLineSegment(sketch, "E245.5", {"start": v(170.8, -105.05) * mm, "end": v(175.05, -100.8) * mm});
            skPoint(sketch, "E245.0.midPoint", {"position": v(177.95, -101.58) * mm});
            skLineSegment(sketch, "E246", {"start": v(177.95, -101.58) * mm, "end": v(176.6, -106.6) * mm, "construction": true});
            skLineSegment(sketch, "E247", {"start": v(176.6, -101.4) * mm, "end": v(176.6, -106.6) * mm, "construction": true});
            skCircle(sketch, "E248", {"center": v(176.6, -106.6) * mm, "radius": 3.25 * mm});
            skCircle(sketch, "E249.cCircle", {"center": v(26.6, -121.6) * mm, "radius": 5.2 * mm, "construction": true});
            skLineSegment(sketch, "E249.0", {"start": v(25.05, -115.8) * mm, "end": v(30.85, -117.35) * mm});
            skLineSegment(sketch, "E249.1", {"start": v(30.85, -117.35) * mm, "end": v(32.4, -123.15) * mm});
            skLineSegment(sketch, "E249.2", {"start": v(32.4, -123.15) * mm, "end": v(28.15, -127.4) * mm});
            skLineSegment(sketch, "E249.3", {"start": v(28.15, -127.4) * mm, "end": v(22.35, -125.85) * mm});
            skLineSegment(sketch, "E249.4", {"start": v(22.35, -125.85) * mm, "end": v(20.8, -120.05) * mm});
            skLineSegment(sketch, "E249.5", {"start": v(20.8, -120.05) * mm, "end": v(25.05, -115.8) * mm});
            skPoint(sketch, "E249.0.midPoint", {"position": v(27.95, -116.58) * mm});
            skLineSegment(sketch, "E250", {"start": v(27.95, -116.58) * mm, "end": v(26.6, -121.6) * mm, "construction": true});
            skLineSegment(sketch, "E251", {"start": v(26.6, -116.4) * mm, "end": v(26.6, -121.6) * mm, "construction": true});
            skCircle(sketch, "E252", {"center": v(26.6, -121.6) * mm, "radius": 3.25 * mm});
            skCircle(sketch, "E253.cCircle", {"center": v(46.6, -121.6) * mm, "radius": 5.2 * mm, "construction": true});
            skLineSegment(sketch, "E253.0", {"start": v(45.05, -115.8) * mm, "end": v(50.85, -117.35) * mm});
            skLineSegment(sketch, "E253.1", {"start": v(50.85, -117.35) * mm, "end": v(52.4, -123.15) * mm});
            skLineSegment(sketch, "E253.2", {"start": v(52.4, -123.15) * mm, "end": v(48.15, -127.4) * mm});
            skLineSegment(sketch, "E253.3", {"start": v(48.15, -127.4) * mm, "end": v(42.35, -125.85) * mm});
            skLineSegment(sketch, "E253.4", {"start": v(42.35, -125.85) * mm, "end": v(40.8, -120.05) * mm});
            skLineSegment(sketch, "E253.5", {"start": v(40.8, -120.05) * mm, "end": v(45.05, -115.8) * mm});
            skPoint(sketch, "E253.0.midPoint", {"position": v(47.95, -116.58) * mm});
            skLineSegment(sketch, "E254", {"start": v(47.95, -116.58) * mm, "end": v(46.6, -121.6) * mm, "construction": true});
            skLineSegment(sketch, "E255", {"start": v(46.6, -116.4) * mm, "end": v(46.6, -121.6) * mm, "construction": true});
            skCircle(sketch, "E256", {"center": v(46.6, -121.6) * mm, "radius": 3.25 * mm});
            skCircle(sketch, "E257.cCircle", {"center": v(61.6, -121.6) * mm, "radius": 5.2 * mm, "construction": true});
            skLineSegment(sketch, "E257.0", {"start": v(60.05, -115.8) * mm, "end": v(65.85, -117.35) * mm});
            skLineSegment(sketch, "E257.1", {"start": v(65.85, -117.35) * mm, "end": v(67.4, -123.15) * mm});
            skLineSegment(sketch, "E257.2", {"start": v(67.4, -123.15) * mm, "end": v(63.15, -127.4) * mm});
            skLineSegment(sketch, "E257.3", {"start": v(63.15, -127.4) * mm, "end": v(57.35, -125.85) * mm});
            skLineSegment(sketch, "E257.4", {"start": v(57.35, -125.85) * mm, "end": v(55.8, -120.05) * mm});
            skLineSegment(sketch, "E257.5", {"start": v(55.8, -120.05) * mm, "end": v(60.05, -115.8) * mm});
            skPoint(sketch, "E257.0.midPoint", {"position": v(62.95, -116.58) * mm});
            skLineSegment(sketch, "E258", {"start": v(62.95, -116.58) * mm, "end": v(61.6, -121.6) * mm, "construction": true});
            skLineSegment(sketch, "E259", {"start": v(61.6, -116.4) * mm, "end": v(61.6, -121.6) * mm, "construction": true});
            skCircle(sketch, "E260", {"center": v(61.6, -121.6) * mm, "radius": 3.25 * mm});
            skCircle(sketch, "E261.cCircle", {"center": v(76.6, -121.6) * mm, "radius": 5.2 * mm, "construction": true});
            skLineSegment(sketch, "E261.0", {"start": v(75.05, -115.8) * mm, "end": v(80.85, -117.35) * mm});
            skLineSegment(sketch, "E261.1", {"start": v(80.85, -117.35) * mm, "end": v(82.4, -123.15) * mm});
            skLineSegment(sketch, "E261.2", {"start": v(82.4, -123.15) * mm, "end": v(78.15, -127.4) * mm});
            skLineSegment(sketch, "E261.3", {"start": v(78.15, -127.4) * mm, "end": v(72.35, -125.85) * mm});
            skLineSegment(sketch, "E261.4", {"start": v(72.35, -125.85) * mm, "end": v(70.8, -120.05) * mm});
            skLineSegment(sketch, "E261.5", {"start": v(70.8, -120.05) * mm, "end": v(75.05, -115.8) * mm});
            skPoint(sketch, "E261.0.midPoint", {"position": v(77.95, -116.58) * mm});
            skLineSegment(sketch, "E262", {"start": v(77.95, -116.58) * mm, "end": v(76.6, -121.6) * mm, "construction": true});
            skLineSegment(sketch, "E263", {"start": v(76.6, -116.4) * mm, "end": v(76.6, -121.6) * mm, "construction": true});
            skCircle(sketch, "E264", {"center": v(76.6, -121.6) * mm, "radius": 3.25 * mm});
            skCircle(sketch, "E265.cCircle", {"center": v(91.6, -121.6) * mm, "radius": 5.2 * mm, "construction": true});
            skLineSegment(sketch, "E265.0", {"start": v(90.05, -115.8) * mm, "end": v(95.85, -117.35) * mm});
            skLineSegment(sketch, "E265.1", {"start": v(95.85, -117.35) * mm, "end": v(97.4, -123.15) * mm});
            skLineSegment(sketch, "E265.2", {"start": v(97.4, -123.15) * mm, "end": v(93.15, -127.4) * mm});
            skLineSegment(sketch, "E265.3", {"start": v(93.15, -127.4) * mm, "end": v(87.35, -125.85) * mm});
            skLineSegment(sketch, "E265.4", {"start": v(87.35, -125.85) * mm, "end": v(85.8, -120.05) * mm});
            skLineSegment(sketch, "E265.5", {"start": v(85.8, -120.05) * mm, "end": v(90.05, -115.8) * mm});
            skPoint(sketch, "E265.0.midPoint", {"position": v(92.95, -116.58) * mm});
            skLineSegment(sketch, "E266", {"start": v(92.95, -116.58) * mm, "end": v(91.6, -121.6) * mm, "construction": true});
            skLineSegment(sketch, "E267", {"start": v(91.6, -116.4) * mm, "end": v(91.6, -121.6) * mm, "construction": true});
            skCircle(sketch, "E268", {"center": v(91.6, -121.6) * mm, "radius": 3.25 * mm});
            skCircle(sketch, "E269.cCircle", {"center": v(106.6, -121.6) * mm, "radius": 5.2 * mm, "construction": true});
            skLineSegment(sketch, "E269.0", {"start": v(105.05, -115.8) * mm, "end": v(110.85, -117.35) * mm});
            skLineSegment(sketch, "E269.1", {"start": v(110.85, -117.35) * mm, "end": v(112.4, -123.15) * mm});
            skLineSegment(sketch, "E269.2", {"start": v(112.4, -123.15) * mm, "end": v(108.15, -127.4) * mm});
            skLineSegment(sketch, "E269.3", {"start": v(108.15, -127.4) * mm, "end": v(102.35, -125.85) * mm});
            skLineSegment(sketch, "E269.4", {"start": v(102.35, -125.85) * mm, "end": v(100.8, -120.05) * mm});
            skLineSegment(sketch, "E269.5", {"start": v(100.8, -120.05) * mm, "end": v(105.05, -115.8) * mm});
            skPoint(sketch, "E269.0.midPoint", {"position": v(107.95, -116.58) * mm});
            skLineSegment(sketch, "E270", {"start": v(107.95, -116.58) * mm, "end": v(106.6, -121.6) * mm, "construction": true});
            skLineSegment(sketch, "E271", {"start": v(106.6, -116.4) * mm, "end": v(106.6, -121.6) * mm, "construction": true});
            skCircle(sketch, "E272", {"center": v(106.6, -121.6) * mm, "radius": 3.25 * mm});
            skCircle(sketch, "E273.cCircle", {"center": v(121.6, -121.6) * mm, "radius": 5.2 * mm, "construction": true});
            skLineSegment(sketch, "E273.0", {"start": v(120.05, -115.8) * mm, "end": v(125.85, -117.35) * mm});
            skLineSegment(sketch, "E273.1", {"start": v(125.85, -117.35) * mm, "end": v(127.4, -123.15) * mm});
            skLineSegment(sketch, "E273.2", {"start": v(127.4, -123.15) * mm, "end": v(123.15, -127.4) * mm});
            skLineSegment(sketch, "E273.3", {"start": v(123.15, -127.4) * mm, "end": v(117.35, -125.85) * mm});
            skLineSegment(sketch, "E273.4", {"start": v(117.35, -125.85) * mm, "end": v(115.8, -120.05) * mm});
            skLineSegment(sketch, "E273.5", {"start": v(115.8, -120.05) * mm, "end": v(120.05, -115.8) * mm});
            skPoint(sketch, "E273.0.midPoint", {"position": v(122.95, -116.58) * mm});
            skLineSegment(sketch, "E274", {"start": v(122.95, -116.58) * mm, "end": v(121.6, -121.6) * mm, "construction": true});
            skLineSegment(sketch, "E275", {"start": v(121.6, -116.4) * mm, "end": v(121.6, -121.6) * mm, "construction": true});
            skCircle(sketch, "E276", {"center": v(121.6, -121.6) * mm, "radius": 3.25 * mm});
            skCircle(sketch, "E277.cCircle", {"center": v(136.6, -121.6) * mm, "radius": 5.2 * mm, "construction": true});
            skLineSegment(sketch, "E277.0", {"start": v(135.05, -115.8) * mm, "end": v(140.85, -117.35) * mm});
            skLineSegment(sketch, "E277.1", {"start": v(140.85, -117.35) * mm, "end": v(142.4, -123.15) * mm});
            skLineSegment(sketch, "E277.2", {"start": v(142.4, -123.15) * mm, "end": v(138.15, -127.4) * mm});
            skLineSegment(sketch, "E277.3", {"start": v(138.15, -127.4) * mm, "end": v(132.35, -125.85) * mm});
            skLineSegment(sketch, "E277.4", {"start": v(132.35, -125.85) * mm, "end": v(130.8, -120.05) * mm});
            skLineSegment(sketch, "E277.5", {"start": v(130.8, -120.05) * mm, "end": v(135.05, -115.8) * mm});
            skPoint(sketch, "E277.0.midPoint", {"position": v(137.95, -116.58) * mm});
            skLineSegment(sketch, "E278", {"start": v(137.95, -116.58) * mm, "end": v(136.6, -121.6) * mm, "construction": true});
            skLineSegment(sketch, "E279", {"start": v(136.6, -116.4) * mm, "end": v(136.6, -121.6) * mm, "construction": true});
            skCircle(sketch, "E280", {"center": v(136.6, -121.6) * mm, "radius": 3.25 * mm});
            skCircle(sketch, "E281.cCircle", {"center": v(151.6, -121.6) * mm, "radius": 5.2 * mm, "construction": true});
            skLineSegment(sketch, "E281.0", {"start": v(150.05, -115.8) * mm, "end": v(155.85, -117.35) * mm});
            skLineSegment(sketch, "E281.1", {"start": v(155.85, -117.35) * mm, "end": v(157.4, -123.15) * mm});
            skLineSegment(sketch, "E281.2", {"start": v(157.4, -123.15) * mm, "end": v(153.15, -127.4) * mm});
            skLineSegment(sketch, "E281.3", {"start": v(153.15, -127.4) * mm, "end": v(147.35, -125.85) * mm});
            skLineSegment(sketch, "E281.4", {"start": v(147.35, -125.85) * mm, "end": v(145.8, -120.05) * mm});
            skLineSegment(sketch, "E281.5", {"start": v(145.8, -120.05) * mm, "end": v(150.05, -115.8) * mm});
            skPoint(sketch, "E281.0.midPoint", {"position": v(152.95, -116.58) * mm});
            skLineSegment(sketch, "E282", {"start": v(152.95, -116.58) * mm, "end": v(151.6, -121.6) * mm, "construction": true});
            skLineSegment(sketch, "E283", {"start": v(151.6, -116.4) * mm, "end": v(151.6, -121.6) * mm, "construction": true});
            skCircle(sketch, "E284", {"center": v(151.6, -121.6) * mm, "radius": 3.25 * mm});
            skCircle(sketch, "E285.cCircle", {"center": v(176.6, -121.6) * mm, "radius": 5.2 * mm, "construction": true});
            skLineSegment(sketch, "E285.0", {"start": v(175.05, -115.8) * mm, "end": v(180.85, -117.35) * mm});
            skLineSegment(sketch, "E285.1", {"start": v(180.85, -117.35) * mm, "end": v(182.4, -123.15) * mm});
            skLineSegment(sketch, "E285.2", {"start": v(182.4, -123.15) * mm, "end": v(178.15, -127.4) * mm});
            skLineSegment(sketch, "E285.3", {"start": v(178.15, -127.4) * mm, "end": v(172.35, -125.85) * mm});
            skLineSegment(sketch, "E285.4", {"start": v(172.35, -125.85) * mm, "end": v(170.8, -120.05) * mm});
            skLineSegment(sketch, "E285.5", {"start": v(170.8, -120.05) * mm, "end": v(175.05, -115.8) * mm});
            skPoint(sketch, "E285.0.midPoint", {"position": v(177.95, -116.58) * mm});
            skLineSegment(sketch, "E286", {"start": v(177.95, -116.58) * mm, "end": v(176.6, -121.6) * mm, "construction": true});
            skLineSegment(sketch, "E287", {"start": v(176.6, -116.4) * mm, "end": v(176.6, -121.6) * mm, "construction": true});
            skCircle(sketch, "E288", {"center": v(176.6, -121.6) * mm, "radius": 3.25 * mm});
            skCircle(sketch, "E289.cCircle", {"center": v(26.6, -136.6) * mm, "radius": 5.2 * mm, "construction": true});
            skLineSegment(sketch, "E289.0", {"start": v(25.05, -130.8) * mm, "end": v(30.85, -132.35) * mm});
            skLineSegment(sketch, "E289.1", {"start": v(30.85, -132.35) * mm, "end": v(32.4, -138.15) * mm});
            skLineSegment(sketch, "E289.2", {"start": v(32.4, -138.15) * mm, "end": v(28.15, -142.4) * mm});
            skLineSegment(sketch, "E289.3", {"start": v(28.15, -142.4) * mm, "end": v(22.35, -140.85) * mm});
            skLineSegment(sketch, "E289.4", {"start": v(22.35, -140.85) * mm, "end": v(20.8, -135.05) * mm});
            skLineSegment(sketch, "E289.5", {"start": v(20.8, -135.05) * mm, "end": v(25.05, -130.8) * mm});
            skPoint(sketch, "E289.0.midPoint", {"position": v(27.95, -131.58) * mm});
            skLineSegment(sketch, "E290", {"start": v(27.95, -131.58) * mm, "end": v(26.6, -136.6) * mm, "construction": true});
            skLineSegment(sketch, "E291", {"start": v(26.6, -131.4) * mm, "end": v(26.6, -136.6) * mm, "construction": true});
            skCircle(sketch, "E292", {"center": v(26.6, -136.6) * mm, "radius": 3.25 * mm});
            skCircle(sketch, "E293.cCircle", {"center": v(46.6, -136.6) * mm, "radius": 5.2 * mm, "construction": true});
            skLineSegment(sketch, "E293.0", {"start": v(45.05, -130.8) * mm, "end": v(50.85, -132.35) * mm});
            skLineSegment(sketch, "E293.1", {"start": v(50.85, -132.35) * mm, "end": v(52.4, -138.15) * mm});
            skLineSegment(sketch, "E293.2", {"start": v(52.4, -138.15) * mm, "end": v(48.15, -142.4) * mm});
            skLineSegment(sketch, "E293.3", {"start": v(48.15, -142.4) * mm, "end": v(42.35, -140.85) * mm});
            skLineSegment(sketch, "E293.4", {"start": v(42.35, -140.85) * mm, "end": v(40.8, -135.05) * mm});
            skLineSegment(sketch, "E293.5", {"start": v(40.8, -135.05) * mm, "end": v(45.05, -130.8) * mm});
            skPoint(sketch, "E293.0.midPoint", {"position": v(47.95, -131.58) * mm});
            skLineSegment(sketch, "E294", {"start": v(47.95, -131.58) * mm, "end": v(46.6, -136.6) * mm, "construction": true});
            skLineSegment(sketch, "E295", {"start": v(46.6, -131.4) * mm, "end": v(46.6, -136.6) * mm, "construction": true});
            skCircle(sketch, "E296", {"center": v(46.6, -136.6) * mm, "radius": 3.25 * mm});
            skCircle(sketch, "E297.cCircle", {"center": v(61.6, -136.6) * mm, "radius": 5.2 * mm, "construction": true});
            skLineSegment(sketch, "E297.0", {"start": v(60.05, -130.8) * mm, "end": v(65.85, -132.35) * mm});
            skLineSegment(sketch, "E297.1", {"start": v(65.85, -132.35) * mm, "end": v(67.4, -138.15) * mm});
            skLineSegment(sketch, "E297.2", {"start": v(67.4, -138.15) * mm, "end": v(63.15, -142.4) * mm});
            skLineSegment(sketch, "E297.3", {"start": v(63.15, -142.4) * mm, "end": v(57.35, -140.85) * mm});
            skLineSegment(sketch, "E297.4", {"start": v(57.35, -140.85) * mm, "end": v(55.8, -135.05) * mm});
            skLineSegment(sketch, "E297.5", {"start": v(55.8, -135.05) * mm, "end": v(60.05, -130.8) * mm});
            skPoint(sketch, "E297.0.midPoint", {"position": v(62.95, -131.58) * mm});
            skLineSegment(sketch, "E298", {"start": v(62.95, -131.58) * mm, "end": v(61.6, -136.6) * mm, "construction": true});
            skLineSegment(sketch, "E299", {"start": v(61.6, -131.4) * mm, "end": v(61.6, -136.6) * mm, "construction": true});
            skCircle(sketch, "E300", {"center": v(61.6, -136.6) * mm, "radius": 3.25 * mm});
            skCircle(sketch, "E301.cCircle", {"center": v(76.6, -136.6) * mm, "radius": 5.2 * mm, "construction": true});
            skLineSegment(sketch, "E301.0", {"start": v(75.05, -130.8) * mm, "end": v(80.85, -132.35) * mm});
            skLineSegment(sketch, "E301.1", {"start": v(80.85, -132.35) * mm, "end": v(82.4, -138.15) * mm});
            skLineSegment(sketch, "E301.2", {"start": v(82.4, -138.15) * mm, "end": v(78.15, -142.4) * mm});
            skLineSegment(sketch, "E301.3", {"start": v(78.15, -142.4) * mm, "end": v(72.35, -140.85) * mm});
            skLineSegment(sketch, "E301.4", {"start": v(72.35, -140.85) * mm, "end": v(70.8, -135.05) * mm});
            skLineSegment(sketch, "E301.5", {"start": v(70.8, -135.05) * mm, "end": v(75.05, -130.8) * mm});
            skPoint(sketch, "E301.0.midPoint", {"position": v(77.95, -131.58) * mm});
            skLineSegment(sketch, "E302", {"start": v(77.95, -131.58) * mm, "end": v(76.6, -136.6) * mm, "construction": true});
            skLineSegment(sketch, "E303", {"start": v(76.6, -131.4) * mm, "end": v(76.6, -136.6) * mm, "construction": true});
            skCircle(sketch, "E304", {"center": v(76.6, -136.6) * mm, "radius": 3.25 * mm});
            skCircle(sketch, "E305.cCircle", {"center": v(91.6, -136.6) * mm, "radius": 5.2 * mm, "construction": true});
            skLineSegment(sketch, "E305.0", {"start": v(90.05, -130.8) * mm, "end": v(95.85, -132.35) * mm});
            skLineSegment(sketch, "E305.1", {"start": v(95.85, -132.35) * mm, "end": v(97.4, -138.15) * mm});
            skLineSegment(sketch, "E305.2", {"start": v(97.4, -138.15) * mm, "end": v(93.15, -142.4) * mm});
            skLineSegment(sketch, "E305.3", {"start": v(93.15, -142.4) * mm, "end": v(87.35, -140.85) * mm});
            skLineSegment(sketch, "E305.4", {"start": v(87.35, -140.85) * mm, "end": v(85.8, -135.05) * mm});
            skLineSegment(sketch, "E305.5", {"start": v(85.8, -135.05) * mm, "end": v(90.05, -130.8) * mm});
            skPoint(sketch, "E305.0.midPoint", {"position": v(92.95, -131.58) * mm});
            skLineSegment(sketch, "E306", {"start": v(92.95, -131.58) * mm, "end": v(91.6, -136.6) * mm, "construction": true});
            skLineSegment(sketch, "E307", {"start": v(91.6, -131.4) * mm, "end": v(91.6, -136.6) * mm, "construction": true});
            skCircle(sketch, "E308", {"center": v(91.6, -136.6) * mm, "radius": 3.25 * mm});
            skCircle(sketch, "E309.cCircle", {"center": v(106.6, -136.6) * mm, "radius": 5.2 * mm, "construction": true});
            skLineSegment(sketch, "E309.0", {"start": v(105.05, -130.8) * mm, "end": v(110.85, -132.35) * mm});
            skLineSegment(sketch, "E309.1", {"start": v(110.85, -132.35) * mm, "end": v(112.4, -138.15) * mm});
            skLineSegment(sketch, "E309.2", {"start": v(112.4, -138.15) * mm, "end": v(108.15, -142.4) * mm});
            skLineSegment(sketch, "E309.3", {"start": v(108.15, -142.4) * mm, "end": v(102.35, -140.85) * mm});
            skLineSegment(sketch, "E309.4", {"start": v(102.35, -140.85) * mm, "end": v(100.8, -135.05) * mm});
            skLineSegment(sketch, "E309.5", {"start": v(100.8, -135.05) * mm, "end": v(105.05, -130.8) * mm});
            skPoint(sketch, "E309.0.midPoint", {"position": v(107.95, -131.58) * mm});
            skLineSegment(sketch, "E310", {"start": v(107.95, -131.58) * mm, "end": v(106.6, -136.6) * mm, "construction": true});
            skLineSegment(sketch, "E311", {"start": v(106.6, -131.4) * mm, "end": v(106.6, -136.6) * mm, "construction": true});
            skCircle(sketch, "E312", {"center": v(106.6, -136.6) * mm, "radius": 3.25 * mm});
            skCircle(sketch, "E313.cCircle", {"center": v(121.6, -136.6) * mm, "radius": 5.2 * mm, "construction": true});
            skLineSegment(sketch, "E313.0", {"start": v(120.05, -130.8) * mm, "end": v(125.85, -132.35) * mm});
            skLineSegment(sketch, "E313.1", {"start": v(125.85, -132.35) * mm, "end": v(127.4, -138.15) * mm});
            skLineSegment(sketch, "E313.2", {"start": v(127.4, -138.15) * mm, "end": v(123.15, -142.4) * mm});
            skLineSegment(sketch, "E313.3", {"start": v(123.15, -142.4) * mm, "end": v(117.35, -140.85) * mm});
            skLineSegment(sketch, "E313.4", {"start": v(117.35, -140.85) * mm, "end": v(115.8, -135.05) * mm});
            skLineSegment(sketch, "E313.5", {"start": v(115.8, -135.05) * mm, "end": v(120.05, -130.8) * mm});
            skPoint(sketch, "E313.0.midPoint", {"position": v(122.95, -131.58) * mm});
            skLineSegment(sketch, "E314", {"start": v(122.95, -131.58) * mm, "end": v(121.6, -136.6) * mm, "construction": true});
            skLineSegment(sketch, "E315", {"start": v(121.6, -131.4) * mm, "end": v(121.6, -136.6) * mm, "construction": true});
            skCircle(sketch, "E316", {"center": v(121.6, -136.6) * mm, "radius": 3.25 * mm});
            skCircle(sketch, "E317.cCircle", {"center": v(136.6, -136.6) * mm, "radius": 5.2 * mm, "construction": true});
            skLineSegment(sketch, "E317.0", {"start": v(135.05, -130.8) * mm, "end": v(140.85, -132.35) * mm});
            skLineSegment(sketch, "E317.1", {"start": v(140.85, -132.35) * mm, "end": v(142.4, -138.15) * mm});
            skLineSegment(sketch, "E317.2", {"start": v(142.4, -138.15) * mm, "end": v(138.15, -142.4) * mm});
            skLineSegment(sketch, "E317.3", {"start": v(138.15, -142.4) * mm, "end": v(132.35, -140.85) * mm});
            skLineSegment(sketch, "E317.4", {"start": v(132.35, -140.85) * mm, "end": v(130.8, -135.05) * mm});
            skLineSegment(sketch, "E317.5", {"start": v(130.8, -135.05) * mm, "end": v(135.05, -130.8) * mm});
            skPoint(sketch, "E317.0.midPoint", {"position": v(137.95, -131.58) * mm});
            skLineSegment(sketch, "E318", {"start": v(137.95, -131.58) * mm, "end": v(136.6, -136.6) * mm, "construction": true});
            skLineSegment(sketch, "E319", {"start": v(136.6, -131.4) * mm, "end": v(136.6, -136.6) * mm, "construction": true});
            skCircle(sketch, "E320", {"center": v(136.6, -136.6) * mm, "radius": 3.25 * mm});
            skCircle(sketch, "E321.cCircle", {"center": v(151.6, -136.6) * mm, "radius": 5.2 * mm, "construction": true});
            skLineSegment(sketch, "E321.0", {"start": v(150.05, -130.8) * mm, "end": v(155.85, -132.35) * mm});
            skLineSegment(sketch, "E321.1", {"start": v(155.85, -132.35) * mm, "end": v(157.4, -138.15) * mm});
            skLineSegment(sketch, "E321.2", {"start": v(157.4, -138.15) * mm, "end": v(153.15, -142.4) * mm});
            skLineSegment(sketch, "E321.3", {"start": v(153.15, -142.4) * mm, "end": v(147.35, -140.85) * mm});
            skLineSegment(sketch, "E321.4", {"start": v(147.35, -140.85) * mm, "end": v(145.8, -135.05) * mm});
            skLineSegment(sketch, "E321.5", {"start": v(145.8, -135.05) * mm, "end": v(150.05, -130.8) * mm});
            skPoint(sketch, "E321.0.midPoint", {"position": v(152.95, -131.58) * mm});
            skLineSegment(sketch, "E322", {"start": v(152.95, -131.58) * mm, "end": v(151.6, -136.6) * mm, "construction": true});
            skLineSegment(sketch, "E323", {"start": v(151.6, -131.4) * mm, "end": v(151.6, -136.6) * mm, "construction": true});
            skCircle(sketch, "E324", {"center": v(151.6, -136.6) * mm, "radius": 3.25 * mm});
            skCircle(sketch, "E325.cCircle", {"center": v(176.6, -136.6) * mm, "radius": 5.2 * mm, "construction": true});
            skLineSegment(sketch, "E325.0", {"start": v(175.05, -130.8) * mm, "end": v(180.85, -132.35) * mm});
            skLineSegment(sketch, "E325.1", {"start": v(180.85, -132.35) * mm, "end": v(182.4, -138.15) * mm});
            skLineSegment(sketch, "E325.2", {"start": v(182.4, -138.15) * mm, "end": v(178.15, -142.4) * mm});
            skLineSegment(sketch, "E325.3", {"start": v(178.15, -142.4) * mm, "end": v(172.35, -140.85) * mm});
            skLineSegment(sketch, "E325.4", {"start": v(172.35, -140.85) * mm, "end": v(170.8, -135.05) * mm});
            skLineSegment(sketch, "E325.5", {"start": v(170.8, -135.05) * mm, "end": v(175.05, -130.8) * mm});
            skPoint(sketch, "E325.0.midPoint", {"position": v(177.95, -131.58) * mm});
            skLineSegment(sketch, "E326", {"start": v(177.95, -131.58) * mm, "end": v(176.6, -136.6) * mm, "construction": true});
            skLineSegment(sketch, "E327", {"start": v(176.6, -131.4) * mm, "end": v(176.6, -136.6) * mm, "construction": true});
            skCircle(sketch, "E328", {"center": v(176.6, -136.6) * mm, "radius": 3.25 * mm});
            skCircle(sketch, "E329.cCircle", {"center": v(26.6, -151.6) * mm, "radius": 5.2 * mm, "construction": true});
            skLineSegment(sketch, "E329.0", {"start": v(25.05, -145.8) * mm, "end": v(30.85, -147.35) * mm});
            skLineSegment(sketch, "E329.1", {"start": v(30.85, -147.35) * mm, "end": v(32.4, -153.15) * mm});
            skLineSegment(sketch, "E329.2", {"start": v(32.4, -153.15) * mm, "end": v(28.15, -157.4) * mm});
            skLineSegment(sketch, "E329.3", {"start": v(28.15, -157.4) * mm, "end": v(22.35, -155.85) * mm});
            skLineSegment(sketch, "E329.4", {"start": v(22.35, -155.85) * mm, "end": v(20.8, -150.05) * mm});
            skLineSegment(sketch, "E329.5", {"start": v(20.8, -150.05) * mm, "end": v(25.05, -145.8) * mm});
            skPoint(sketch, "E329.0.midPoint", {"position": v(27.95, -146.58) * mm});
            skLineSegment(sketch, "E330", {"start": v(27.95, -146.58) * mm, "end": v(26.6, -151.6) * mm, "construction": true});
            skLineSegment(sketch, "E331", {"start": v(26.6, -146.4) * mm, "end": v(26.6, -151.6) * mm, "construction": true});
            skCircle(sketch, "E332", {"center": v(26.6, -151.6) * mm, "radius": 3.25 * mm});
            skCircle(sketch, "E333.cCircle", {"center": v(46.6, -151.6) * mm, "radius": 5.2 * mm, "construction": true});
            skLineSegment(sketch, "E333.0", {"start": v(45.05, -145.8) * mm, "end": v(50.85, -147.35) * mm});
            skLineSegment(sketch, "E333.1", {"start": v(50.85, -147.35) * mm, "end": v(52.4, -153.15) * mm});
            skLineSegment(sketch, "E333.2", {"start": v(52.4, -153.15) * mm, "end": v(48.15, -157.4) * mm});
            skLineSegment(sketch, "E333.3", {"start": v(48.15, -157.4) * mm, "end": v(42.35, -155.85) * mm});
            skLineSegment(sketch, "E333.4", {"start": v(42.35, -155.85) * mm, "end": v(40.8, -150.05) * mm});
            skLineSegment(sketch, "E333.5", {"start": v(40.8, -150.05) * mm, "end": v(45.05, -145.8) * mm});
            skPoint(sketch, "E333.0.midPoint", {"position": v(47.95, -146.58) * mm});
            skLineSegment(sketch, "E334", {"start": v(47.95, -146.58) * mm, "end": v(46.6, -151.6) * mm, "construction": true});
            skLineSegment(sketch, "E335", {"start": v(46.6, -146.4) * mm, "end": v(46.6, -151.6) * mm, "construction": true});
            skCircle(sketch, "E336", {"center": v(46.6, -151.6) * mm, "radius": 3.25 * mm});
            skCircle(sketch, "E337.cCircle", {"center": v(61.6, -151.6) * mm, "radius": 5.2 * mm, "construction": true});
            skLineSegment(sketch, "E337.0", {"start": v(60.05, -145.8) * mm, "end": v(65.85, -147.35) * mm});
            skLineSegment(sketch, "E337.1", {"start": v(65.85, -147.35) * mm, "end": v(67.4, -153.15) * mm});
            skLineSegment(sketch, "E337.2", {"start": v(67.4, -153.15) * mm, "end": v(63.15, -157.4) * mm});
            skLineSegment(sketch, "E337.3", {"start": v(63.15, -157.4) * mm, "end": v(57.35, -155.85) * mm});
            skLineSegment(sketch, "E337.4", {"start": v(57.35, -155.85) * mm, "end": v(55.8, -150.05) * mm});
            skLineSegment(sketch, "E337.5", {"start": v(55.8, -150.05) * mm, "end": v(60.05, -145.8) * mm});
            skPoint(sketch, "E337.0.midPoint", {"position": v(62.95, -146.58) * mm});
            skLineSegment(sketch, "E338", {"start": v(62.95, -146.58) * mm, "end": v(61.6, -151.6) * mm, "construction": true});
            skLineSegment(sketch, "E339", {"start": v(61.6, -146.4) * mm, "end": v(61.6, -151.6) * mm, "construction": true});
            skCircle(sketch, "E340", {"center": v(61.6, -151.6) * mm, "radius": 3.25 * mm});
            skCircle(sketch, "E341.cCircle", {"center": v(76.6, -151.6) * mm, "radius": 5.2 * mm, "construction": true});
            skLineSegment(sketch, "E341.0", {"start": v(75.05, -145.8) * mm, "end": v(80.85, -147.35) * mm});
            skLineSegment(sketch, "E341.1", {"start": v(80.85, -147.35) * mm, "end": v(82.4, -153.15) * mm});
            skLineSegment(sketch, "E341.2", {"start": v(82.4, -153.15) * mm, "end": v(78.15, -157.4) * mm});
            skLineSegment(sketch, "E341.3", {"start": v(78.15, -157.4) * mm, "end": v(72.35, -155.85) * mm});
            skLineSegment(sketch, "E341.4", {"start": v(72.35, -155.85) * mm, "end": v(70.8, -150.05) * mm});
            skLineSegment(sketch, "E341.5", {"start": v(70.8, -150.05) * mm, "end": v(75.05, -145.8) * mm});
            skPoint(sketch, "E341.0.midPoint", {"position": v(77.95, -146.58) * mm});
            skLineSegment(sketch, "E342", {"start": v(77.95, -146.58) * mm, "end": v(76.6, -151.6) * mm, "construction": true});
            skLineSegment(sketch, "E343", {"start": v(76.6, -146.4) * mm, "end": v(76.6, -151.6) * mm, "construction": true});
            skCircle(sketch, "E344", {"center": v(76.6, -151.6) * mm, "radius": 3.25 * mm});
            skCircle(sketch, "E345.cCircle", {"center": v(91.6, -151.6) * mm, "radius": 5.2 * mm, "construction": true});
            skLineSegment(sketch, "E345.0", {"start": v(90.05, -145.8) * mm, "end": v(95.85, -147.35) * mm});
            skLineSegment(sketch, "E345.1", {"start": v(95.85, -147.35) * mm, "end": v(97.4, -153.15) * mm});
            skLineSegment(sketch, "E345.2", {"start": v(97.4, -153.15) * mm, "end": v(93.15, -157.4) * mm});
            skLineSegment(sketch, "E345.3", {"start": v(93.15, -157.4) * mm, "end": v(87.35, -155.85) * mm});
            skLineSegment(sketch, "E345.4", {"start": v(87.35, -155.85) * mm, "end": v(85.8, -150.05) * mm});
            skLineSegment(sketch, "E345.5", {"start": v(85.8, -150.05) * mm, "end": v(90.05, -145.8) * mm});
            skPoint(sketch, "E345.0.midPoint", {"position": v(92.95, -146.58) * mm});
            skLineSegment(sketch, "E346", {"start": v(92.95, -146.58) * mm, "end": v(91.6, -151.6) * mm, "construction": true});
            skLineSegment(sketch, "E347", {"start": v(91.6, -146.4) * mm, "end": v(91.6, -151.6) * mm, "construction": true});
            skCircle(sketch, "E348", {"center": v(91.6, -151.6) * mm, "radius": 3.25 * mm});
            skCircle(sketch, "E349.cCircle", {"center": v(106.6, -151.6) * mm, "radius": 5.2 * mm, "construction": true});
            skLineSegment(sketch, "E349.0", {"start": v(105.05, -145.8) * mm, "end": v(110.85, -147.35) * mm});
            skLineSegment(sketch, "E349.1", {"start": v(110.85, -147.35) * mm, "end": v(112.4, -153.15) * mm});
            skLineSegment(sketch, "E349.2", {"start": v(112.4, -153.15) * mm, "end": v(108.15, -157.4) * mm});
            skLineSegment(sketch, "E349.3", {"start": v(108.15, -157.4) * mm, "end": v(102.35, -155.85) * mm});
            skLineSegment(sketch, "E349.4", {"start": v(102.35, -155.85) * mm, "end": v(100.8, -150.05) * mm});
            skLineSegment(sketch, "E349.5", {"start": v(100.8, -150.05) * mm, "end": v(105.05, -145.8) * mm});
            skPoint(sketch, "E349.0.midPoint", {"position": v(107.95, -146.58) * mm});
            skLineSegment(sketch, "E350", {"start": v(107.95, -146.58) * mm, "end": v(106.6, -151.6) * mm, "construction": true});
            skLineSegment(sketch, "E351", {"start": v(106.6, -146.4) * mm, "end": v(106.6, -151.6) * mm, "construction": true});
            skCircle(sketch, "E352", {"center": v(106.6, -151.6) * mm, "radius": 3.25 * mm});
            skCircle(sketch, "E353.cCircle", {"center": v(121.6, -151.6) * mm, "radius": 5.2 * mm, "construction": true});
            skLineSegment(sketch, "E353.0", {"start": v(120.05, -145.8) * mm, "end": v(125.85, -147.35) * mm});
            skLineSegment(sketch, "E353.1", {"start": v(125.85, -147.35) * mm, "end": v(127.4, -153.15) * mm});
            skLineSegment(sketch, "E353.2", {"start": v(127.4, -153.15) * mm, "end": v(123.15, -157.4) * mm});
            skLineSegment(sketch, "E353.3", {"start": v(123.15, -157.4) * mm, "end": v(117.35, -155.85) * mm});
            skLineSegment(sketch, "E353.4", {"start": v(117.35, -155.85) * mm, "end": v(115.8, -150.05) * mm});
            skLineSegment(sketch, "E353.5", {"start": v(115.8, -150.05) * mm, "end": v(120.05, -145.8) * mm});
            skPoint(sketch, "E353.0.midPoint", {"position": v(122.95, -146.58) * mm});
            skLineSegment(sketch, "E354", {"start": v(122.95, -146.58) * mm, "end": v(121.6, -151.6) * mm, "construction": true});
            skLineSegment(sketch, "E355", {"start": v(121.6, -146.4) * mm, "end": v(121.6, -151.6) * mm, "construction": true});
            skCircle(sketch, "E356", {"center": v(121.6, -151.6) * mm, "radius": 3.25 * mm});
            skCircle(sketch, "E357.cCircle", {"center": v(136.6, -151.6) * mm, "radius": 5.2 * mm, "construction": true});
            skLineSegment(sketch, "E357.0", {"start": v(135.05, -145.8) * mm, "end": v(140.85, -147.35) * mm});
            skLineSegment(sketch, "E357.1", {"start": v(140.85, -147.35) * mm, "end": v(142.4, -153.15) * mm});
            skLineSegment(sketch, "E357.2", {"start": v(142.4, -153.15) * mm, "end": v(138.15, -157.4) * mm});
            skLineSegment(sketch, "E357.3", {"start": v(138.15, -157.4) * mm, "end": v(132.35, -155.85) * mm});
            skLineSegment(sketch, "E357.4", {"start": v(132.35, -155.85) * mm, "end": v(130.8, -150.05) * mm});
            skLineSegment(sketch, "E357.5", {"start": v(130.8, -150.05) * mm, "end": v(135.05, -145.8) * mm});
            skPoint(sketch, "E357.0.midPoint", {"position": v(137.95, -146.58) * mm});
            skLineSegment(sketch, "E358", {"start": v(137.95, -146.58) * mm, "end": v(136.6, -151.6) * mm, "construction": true});
            skLineSegment(sketch, "E359", {"start": v(136.6, -146.4) * mm, "end": v(136.6, -151.6) * mm, "construction": true});
            skCircle(sketch, "E360", {"center": v(136.6, -151.6) * mm, "radius": 3.25 * mm});
            skCircle(sketch, "E361.cCircle", {"center": v(151.6, -151.6) * mm, "radius": 5.2 * mm, "construction": true});
            skLineSegment(sketch, "E361.0", {"start": v(150.05, -145.8) * mm, "end": v(155.85, -147.35) * mm});
            skLineSegment(sketch, "E361.1", {"start": v(155.85, -147.35) * mm, "end": v(157.4, -153.15) * mm});
            skLineSegment(sketch, "E361.2", {"start": v(157.4, -153.15) * mm, "end": v(153.15, -157.4) * mm});
            skLineSegment(sketch, "E361.3", {"start": v(153.15, -157.4) * mm, "end": v(147.35, -155.85) * mm});
            skLineSegment(sketch, "E361.4", {"start": v(147.35, -155.85) * mm, "end": v(145.8, -150.05) * mm});
            skLineSegment(sketch, "E361.5", {"start": v(145.8, -150.05) * mm, "end": v(150.05, -145.8) * mm});
            skPoint(sketch, "E361.0.midPoint", {"position": v(152.95, -146.58) * mm});
            skLineSegment(sketch, "E362", {"start": v(152.95, -146.58) * mm, "end": v(151.6, -151.6) * mm, "construction": true});
            skLineSegment(sketch, "E363", {"start": v(151.6, -146.4) * mm, "end": v(151.6, -151.6) * mm, "construction": true});
            skCircle(sketch, "E364", {"center": v(151.6, -151.6) * mm, "radius": 3.25 * mm});
            skCircle(sketch, "E365.cCircle", {"center": v(176.6, -151.6) * mm, "radius": 5.2 * mm, "construction": true});
            skLineSegment(sketch, "E365.0", {"start": v(175.05, -145.8) * mm, "end": v(180.85, -147.35) * mm});
            skLineSegment(sketch, "E365.1", {"start": v(180.85, -147.35) * mm, "end": v(182.4, -153.15) * mm});
            skLineSegment(sketch, "E365.2", {"start": v(182.4, -153.15) * mm, "end": v(178.15, -157.4) * mm});
            skLineSegment(sketch, "E365.3", {"start": v(178.15, -157.4) * mm, "end": v(172.35, -155.85) * mm});
            skLineSegment(sketch, "E365.4", {"start": v(172.35, -155.85) * mm, "end": v(170.8, -150.05) * mm});
            skLineSegment(sketch, "E365.5", {"start": v(170.8, -150.05) * mm, "end": v(175.05, -145.8) * mm});
            skPoint(sketch, "E365.0.midPoint", {"position": v(177.95, -146.58) * mm});
            skLineSegment(sketch, "E366", {"start": v(177.95, -146.58) * mm, "end": v(176.6, -151.6) * mm, "construction": true});
            skLineSegment(sketch, "E367", {"start": v(176.6, -146.4) * mm, "end": v(176.6, -151.6) * mm, "construction": true});
            skCircle(sketch, "E368", {"center": v(176.6, -151.6) * mm, "radius": 3.25 * mm});
            skCircle(sketch, "E369.cCircle", {"center": v(26.6, -176.6) * mm, "radius": 5.2 * mm, "construction": true});
            skLineSegment(sketch, "E369.0", {"start": v(25.05, -170.8) * mm, "end": v(30.85, -172.35) * mm});
            skLineSegment(sketch, "E369.1", {"start": v(30.85, -172.35) * mm, "end": v(32.4, -178.15) * mm});
            skLineSegment(sketch, "E369.2", {"start": v(32.4, -178.15) * mm, "end": v(28.15, -182.4) * mm});
            skLineSegment(sketch, "E369.3", {"start": v(28.15, -182.4) * mm, "end": v(22.35, -180.85) * mm});
            skLineSegment(sketch, "E369.4", {"start": v(22.35, -180.85) * mm, "end": v(20.8, -175.05) * mm});
            skLineSegment(sketch, "E369.5", {"start": v(20.8, -175.05) * mm, "end": v(25.05, -170.8) * mm});
            skPoint(sketch, "E369.0.midPoint", {"position": v(27.95, -171.58) * mm});
            skLineSegment(sketch, "E370", {"start": v(27.95, -171.58) * mm, "end": v(26.6, -176.6) * mm, "construction": true});
            skLineSegment(sketch, "E371", {"start": v(26.6, -171.4) * mm, "end": v(26.6, -176.6) * mm, "construction": true});
            skCircle(sketch, "E372", {"center": v(26.6, -176.6) * mm, "radius": 3.25 * mm});
            skCircle(sketch, "E373.cCircle", {"center": v(46.6, -176.6) * mm, "radius": 5.2 * mm, "construction": true});
            skLineSegment(sketch, "E373.0", {"start": v(45.05, -170.8) * mm, "end": v(50.85, -172.35) * mm});
            skLineSegment(sketch, "E373.1", {"start": v(50.85, -172.35) * mm, "end": v(52.4, -178.15) * mm});
            skLineSegment(sketch, "E373.2", {"start": v(52.4, -178.15) * mm, "end": v(48.15, -182.4) * mm});
            skLineSegment(sketch, "E373.3", {"start": v(48.15, -182.4) * mm, "end": v(42.35, -180.85) * mm});
            skLineSegment(sketch, "E373.4", {"start": v(42.35, -180.85) * mm, "end": v(40.8, -175.05) * mm});
            skLineSegment(sketch, "E373.5", {"start": v(40.8, -175.05) * mm, "end": v(45.05, -170.8) * mm});
            skPoint(sketch, "E373.0.midPoint", {"position": v(47.95, -171.58) * mm});
            skLineSegment(sketch, "E374", {"start": v(47.95, -171.58) * mm, "end": v(46.6, -176.6) * mm, "construction": true});
            skLineSegment(sketch, "E375", {"start": v(46.6, -171.4) * mm, "end": v(46.6, -176.6) * mm, "construction": true});
            skCircle(sketch, "E376", {"center": v(46.6, -176.6) * mm, "radius": 3.25 * mm});
            skCircle(sketch, "E377.cCircle", {"center": v(61.6, -176.6) * mm, "radius": 5.2 * mm, "construction": true});
            skLineSegment(sketch, "E377.0", {"start": v(60.05, -170.8) * mm, "end": v(65.85, -172.35) * mm});
            skLineSegment(sketch, "E377.1", {"start": v(65.85, -172.35) * mm, "end": v(67.4, -178.15) * mm});
            skLineSegment(sketch, "E377.2", {"start": v(67.4, -178.15) * mm, "end": v(63.15, -182.4) * mm});
            skLineSegment(sketch, "E377.3", {"start": v(63.15, -182.4) * mm, "end": v(57.35, -180.85) * mm});
            skLineSegment(sketch, "E377.4", {"start": v(57.35, -180.85) * mm, "end": v(55.8, -175.05) * mm});
            skLineSegment(sketch, "E377.5", {"start": v(55.8, -175.05) * mm, "end": v(60.05, -170.8) * mm});
            skPoint(sketch, "E377.0.midPoint", {"position": v(62.95, -171.58) * mm});
            skLineSegment(sketch, "E378", {"start": v(62.95, -171.58) * mm, "end": v(61.6, -176.6) * mm, "construction": true});
            skLineSegment(sketch, "E379", {"start": v(61.6, -171.4) * mm, "end": v(61.6, -176.6) * mm, "construction": true});
            skCircle(sketch, "E380", {"center": v(61.6, -176.6) * mm, "radius": 3.25 * mm});
            skCircle(sketch, "E381.cCircle", {"center": v(76.6, -176.6) * mm, "radius": 5.2 * mm, "construction": true});
            skLineSegment(sketch, "E381.0", {"start": v(75.05, -170.8) * mm, "end": v(80.85, -172.35) * mm});
            skLineSegment(sketch, "E381.1", {"start": v(80.85, -172.35) * mm, "end": v(82.4, -178.15) * mm});
            skLineSegment(sketch, "E381.2", {"start": v(82.4, -178.15) * mm, "end": v(78.15, -182.4) * mm});
            skLineSegment(sketch, "E381.3", {"start": v(78.15, -182.4) * mm, "end": v(72.35, -180.85) * mm});
            skLineSegment(sketch, "E381.4", {"start": v(72.35, -180.85) * mm, "end": v(70.8, -175.05) * mm});
            skLineSegment(sketch, "E381.5", {"start": v(70.8, -175.05) * mm, "end": v(75.05, -170.8) * mm});
            skPoint(sketch, "E381.0.midPoint", {"position": v(77.95, -171.58) * mm});
            skLineSegment(sketch, "E382", {"start": v(77.95, -171.58) * mm, "end": v(76.6, -176.6) * mm, "construction": true});
            skLineSegment(sketch, "E383", {"start": v(76.6, -171.4) * mm, "end": v(76.6, -176.6) * mm, "construction": true});
            skCircle(sketch, "E384", {"center": v(76.6, -176.6) * mm, "radius": 3.25 * mm});
            skCircle(sketch, "E385.cCircle", {"center": v(91.6, -176.6) * mm, "radius": 5.2 * mm, "construction": true});
            skLineSegment(sketch, "E385.0", {"start": v(90.05, -170.8) * mm, "end": v(95.85, -172.35) * mm});
            skLineSegment(sketch, "E385.1", {"start": v(95.85, -172.35) * mm, "end": v(97.4, -178.15) * mm});
            skLineSegment(sketch, "E385.2", {"start": v(97.4, -178.15) * mm, "end": v(93.15, -182.4) * mm});
            skLineSegment(sketch, "E385.3", {"start": v(93.15, -182.4) * mm, "end": v(87.35, -180.85) * mm});
            skLineSegment(sketch, "E385.4", {"start": v(87.35, -180.85) * mm, "end": v(85.8, -175.05) * mm});
            skLineSegment(sketch, "E385.5", {"start": v(85.8, -175.05) * mm, "end": v(90.05, -170.8) * mm});
            skPoint(sketch, "E385.0.midPoint", {"position": v(92.95, -171.58) * mm});
            skLineSegment(sketch, "E386", {"start": v(92.95, -171.58) * mm, "end": v(91.6, -176.6) * mm, "construction": true});
            skLineSegment(sketch, "E387", {"start": v(91.6, -171.4) * mm, "end": v(91.6, -176.6) * mm, "construction": true});
            skCircle(sketch, "E388", {"center": v(91.6, -176.6) * mm, "radius": 3.25 * mm});
            skCircle(sketch, "E389.cCircle", {"center": v(106.6, -176.6) * mm, "radius": 5.2 * mm, "construction": true});
            skLineSegment(sketch, "E389.0", {"start": v(105.05, -170.8) * mm, "end": v(110.85, -172.35) * mm});
            skLineSegment(sketch, "E389.1", {"start": v(110.85, -172.35) * mm, "end": v(112.4, -178.15) * mm});
            skLineSegment(sketch, "E389.2", {"start": v(112.4, -178.15) * mm, "end": v(108.15, -182.4) * mm});
            skLineSegment(sketch, "E389.3", {"start": v(108.15, -182.4) * mm, "end": v(102.35, -180.85) * mm});
            skLineSegment(sketch, "E389.4", {"start": v(102.35, -180.85) * mm, "end": v(100.8, -175.05) * mm});
            skLineSegment(sketch, "E389.5", {"start": v(100.8, -175.05) * mm, "end": v(105.05, -170.8) * mm});
            skPoint(sketch, "E389.0.midPoint", {"position": v(107.95, -171.58) * mm});
            skLineSegment(sketch, "E390", {"start": v(107.95, -171.58) * mm, "end": v(106.6, -176.6) * mm, "construction": true});
            skLineSegment(sketch, "E391", {"start": v(106.6, -171.4) * mm, "end": v(106.6, -176.6) * mm, "construction": true});
            skCircle(sketch, "E392", {"center": v(106.6, -176.6) * mm, "radius": 3.25 * mm});
            skCircle(sketch, "E393.cCircle", {"center": v(121.6, -176.6) * mm, "radius": 5.2 * mm, "construction": true});
            skLineSegment(sketch, "E393.0", {"start": v(120.05, -170.8) * mm, "end": v(125.85, -172.35) * mm});
            skLineSegment(sketch, "E393.1", {"start": v(125.85, -172.35) * mm, "end": v(127.4, -178.15) * mm});
            skLineSegment(sketch, "E393.2", {"start": v(127.4, -178.15) * mm, "end": v(123.15, -182.4) * mm});
            skLineSegment(sketch, "E393.3", {"start": v(123.15, -182.4) * mm, "end": v(117.35, -180.85) * mm});
            skLineSegment(sketch, "E393.4", {"start": v(117.35, -180.85) * mm, "end": v(115.8, -175.05) * mm});
            skLineSegment(sketch, "E393.5", {"start": v(115.8, -175.05) * mm, "end": v(120.05, -170.8) * mm});
            skPoint(sketch, "E393.0.midPoint", {"position": v(122.95, -171.58) * mm});
            skLineSegment(sketch, "E394", {"start": v(122.95, -171.58) * mm, "end": v(121.6, -176.6) * mm, "construction": true});
            skLineSegment(sketch, "E395", {"start": v(121.6, -171.4) * mm, "end": v(121.6, -176.6) * mm, "construction": true});
            skCircle(sketch, "E396", {"center": v(121.6, -176.6) * mm, "radius": 3.25 * mm});
            skCircle(sketch, "E397.cCircle", {"center": v(136.6, -176.6) * mm, "radius": 5.2 * mm, "construction": true});
            skLineSegment(sketch, "E397.0", {"start": v(135.05, -170.8) * mm, "end": v(140.85, -172.35) * mm});
            skLineSegment(sketch, "E397.1", {"start": v(140.85, -172.35) * mm, "end": v(142.4, -178.15) * mm});
            skLineSegment(sketch, "E397.2", {"start": v(142.4, -178.15) * mm, "end": v(138.15, -182.4) * mm});
            skLineSegment(sketch, "E397.3", {"start": v(138.15, -182.4) * mm, "end": v(132.35, -180.85) * mm});
            skLineSegment(sketch, "E397.4", {"start": v(132.35, -180.85) * mm, "end": v(130.8, -175.05) * mm});
            skLineSegment(sketch, "E397.5", {"start": v(130.8, -175.05) * mm, "end": v(135.05, -170.8) * mm});
            skPoint(sketch, "E397.0.midPoint", {"position": v(137.95, -171.58) * mm});
            skLineSegment(sketch, "E398", {"start": v(137.95, -171.58) * mm, "end": v(136.6, -176.6) * mm, "construction": true});
            skLineSegment(sketch, "E399", {"start": v(136.6, -171.4) * mm, "end": v(136.6, -176.6) * mm, "construction": true});
            skCircle(sketch, "E400", {"center": v(136.6, -176.6) * mm, "radius": 3.25 * mm});
            skCircle(sketch, "E401.cCircle", {"center": v(151.6, -176.6) * mm, "radius": 5.2 * mm, "construction": true});
            skLineSegment(sketch, "E401.0", {"start": v(150.05, -170.8) * mm, "end": v(155.85, -172.35) * mm});
            skLineSegment(sketch, "E401.1", {"start": v(155.85, -172.35) * mm, "end": v(157.4, -178.15) * mm});
            skLineSegment(sketch, "E401.2", {"start": v(157.4, -178.15) * mm, "end": v(153.15, -182.4) * mm});
            skLineSegment(sketch, "E401.3", {"start": v(153.15, -182.4) * mm, "end": v(147.35, -180.85) * mm});
            skLineSegment(sketch, "E401.4", {"start": v(147.35, -180.85) * mm, "end": v(145.8, -175.05) * mm});
            skLineSegment(sketch, "E401.5", {"start": v(145.8, -175.05) * mm, "end": v(150.05, -170.8) * mm});
            skPoint(sketch, "E401.0.midPoint", {"position": v(152.95, -171.58) * mm});
            skLineSegment(sketch, "E402", {"start": v(152.95, -171.58) * mm, "end": v(151.6, -176.6) * mm, "construction": true});
            skLineSegment(sketch, "E403", {"start": v(151.6, -171.4) * mm, "end": v(151.6, -176.6) * mm, "construction": true});
            skCircle(sketch, "E404", {"center": v(151.6, -176.6) * mm, "radius": 3.25 * mm});
            skCircle(sketch, "E405.cCircle", {"center": v(176.6, -176.6) * mm, "radius": 5.2 * mm, "construction": true});
            skLineSegment(sketch, "E405.0", {"start": v(175.05, -170.8) * mm, "end": v(180.85, -172.35) * mm});
            skLineSegment(sketch, "E405.1", {"start": v(180.85, -172.35) * mm, "end": v(182.4, -178.15) * mm});
            skLineSegment(sketch, "E405.2", {"start": v(182.4, -178.15) * mm, "end": v(178.15, -182.4) * mm});
            skLineSegment(sketch, "E405.3", {"start": v(178.15, -182.4) * mm, "end": v(172.35, -180.85) * mm});
            skLineSegment(sketch, "E405.4", {"start": v(172.35, -180.85) * mm, "end": v(170.8, -175.05) * mm});
            skLineSegment(sketch, "E405.5", {"start": v(170.8, -175.05) * mm, "end": v(175.05, -170.8) * mm});
            skPoint(sketch, "E405.0.midPoint", {"position": v(177.95, -171.58) * mm});
            skLineSegment(sketch, "E406", {"start": v(177.95, -171.58) * mm, "end": v(176.6, -176.6) * mm, "construction": true});
            skLineSegment(sketch, "E407", {"start": v(176.6, -171.4) * mm, "end": v(176.6, -176.6) * mm, "construction": true});
            skCircle(sketch, "E408", {"center": v(176.6, -176.6) * mm, "radius": 3.25 * mm});
            skLineSegment(sketch, "E409", {"start": v(26.6, 0) * mm, "end": v(26.6, -26.6) * mm, "construction": true});
            skLineSegment(sketch, "E410", {"start": v(0, -26.6) * mm, "end": v(26.6, -26.6) * mm, "construction": true});
            skLineSegment(sketch, "E411", {"start": v(203.2, -176.6) * mm, "end": v(176.6, -176.6) * mm, "construction": true});
            skLineSegment(sketch, "E412", {"start": v(176.6, -203.2) * mm, "end": v(176.6, -176.6) * mm, "construction": true});
            skSolve(sketch);
        }
        {
            var Q0;
            Q0=makeQuery(id+"F6.imprint","IMPRINT",FACE,{"disambiguationData":[TD([[makeQuery(id+"F6.imprint","IMPRINT",EDGE,{"derivedFrom":sQuery(id+"F6.wireOp",EDGE,"E12")}),1.0]])]});
            var Q1;
            Q1=makeQuery(id+"F6.imprint","IMPRINT",FACE,{"disambiguationData":[TD([[makeQuery(id+"F6.imprint","IMPRINT",EDGE,{"derivedFrom":sQuery(id+"F6.wireOp",EDGE,"E16")}),1.0]])]});
            var Q2;
            Q2=makeQuery(id+"F6.imprint","IMPRINT",FACE,{"disambiguationData":[TD([[makeQuery(id+"F6.imprint","IMPRINT",EDGE,{"derivedFrom":sQuery(id+"F6.wireOp",EDGE,"E20")}),1.0]])]});
            var Q3;
            Q3=makeQuery(id+"F6.imprint","IMPRINT",FACE,{"disambiguationData":[TD([[makeQuery(id+"F6.imprint","IMPRINT",EDGE,{"derivedFrom":sQuery(id+"F6.wireOp",EDGE,"E24")}),1.0]])]});
            var Q4;
            Q4=makeQuery(id+"F6.imprint","IMPRINT",FACE,{"disambiguationData":[TD([[makeQuery(id+"F6.imprint","IMPRINT",EDGE,{"derivedFrom":sQuery(id+"F6.wireOp",EDGE,"E28")}),1.0]])]});
            var Q5;
            Q5=makeQuery(id+"F6.imprint","IMPRINT",FACE,{"disambiguationData":[TD([[makeQuery(id+"F6.imprint","IMPRINT",EDGE,{"derivedFrom":sQuery(id+"F6.wireOp",EDGE,"E32")}),1.0]])]});
            var Q6;
            Q6=makeQuery(id+"F6.imprint","IMPRINT",FACE,{"disambiguationData":[TD([[makeQuery(id+"F6.imprint","IMPRINT",EDGE,{"derivedFrom":sQuery(id+"F6.wireOp",EDGE,"E36")}),1.0]])]});
            var Q7;
            Q7=makeQuery(id+"F6.imprint","IMPRINT",FACE,{"disambiguationData":[TD([[makeQuery(id+"F6.imprint","IMPRINT",EDGE,{"derivedFrom":sQuery(id+"F6.wireOp",EDGE,"E40")}),1.0]])]});
            var Q8;
            Q8=makeQuery(id+"F6.imprint","IMPRINT",FACE,{"disambiguationData":[TD([[makeQuery(id+"F6.imprint","IMPRINT",EDGE,{"derivedFrom":sQuery(id+"F6.wireOp",EDGE,"E44")}),1.0]])]});
            var Q9;
            Q9=makeQuery(id+"F6.imprint","IMPRINT",FACE,{"disambiguationData":[TD([[makeQuery(id+"F6.imprint","IMPRINT",EDGE,{"derivedFrom":sQuery(id+"F6.wireOp",EDGE,"E48")}),1.0]])]});
            var Q10;
            Q10=makeQuery(id+"F6.imprint","IMPRINT",FACE,{"disambiguationData":[TD([[makeQuery(id+"F6.imprint","IMPRINT",EDGE,{"derivedFrom":sQuery(id+"F6.wireOp",EDGE,"E88")}),1.0]])]});
            var Q11;
            Q11=makeQuery(id+"F6.imprint","IMPRINT",FACE,{"disambiguationData":[TD([[makeQuery(id+"F6.imprint","IMPRINT",EDGE,{"derivedFrom":sQuery(id+"F6.wireOp",EDGE,"E84")}),1.0]])]});
            var Q12;
            Q12=makeQuery(id+"F6.imprint","IMPRINT",FACE,{"disambiguationData":[TD([[makeQuery(id+"F6.imprint","IMPRINT",EDGE,{"derivedFrom":sQuery(id+"F6.wireOp",EDGE,"E80")}),1.0]])]});
            var Q13;
            Q13=makeQuery(id+"F6.imprint","IMPRINT",FACE,{"disambiguationData":[TD([[makeQuery(id+"F6.imprint","IMPRINT",EDGE,{"derivedFrom":sQuery(id+"F6.wireOp",EDGE,"E76")}),1.0]])]});
            var Q14;
            Q14=makeQuery(id+"F6.imprint","IMPRINT",FACE,{"disambiguationData":[TD([[makeQuery(id+"F6.imprint","IMPRINT",EDGE,{"derivedFrom":sQuery(id+"F6.wireOp",EDGE,"E72")}),1.0]])]});
            var Q15;
            Q15=makeQuery(id+"F6.imprint","IMPRINT",FACE,{"disambiguationData":[TD([[makeQuery(id+"F6.imprint","IMPRINT",EDGE,{"derivedFrom":sQuery(id+"F6.wireOp",EDGE,"E68")}),1.0]])]});
            var Q16;
            Q16=makeQuery(id+"F6.imprint","IMPRINT",FACE,{"disambiguationData":[TD([[makeQuery(id+"F6.imprint","IMPRINT",EDGE,{"derivedFrom":sQuery(id+"F6.wireOp",EDGE,"E64")}),1.0]])]});
            var Q17;
            Q17=makeQuery(id+"F6.imprint","IMPRINT",FACE,{"disambiguationData":[TD([[makeQuery(id+"F6.imprint","IMPRINT",EDGE,{"derivedFrom":sQuery(id+"F6.wireOp",EDGE,"E60")}),1.0]])]});
            var Q18;
            Q18=makeQuery(id+"F6.imprint","IMPRINT",FACE,{"disambiguationData":[TD([[makeQuery(id+"F6.imprint","IMPRINT",EDGE,{"derivedFrom":sQuery(id+"F6.wireOp",EDGE,"E56")}),1.0]])]});
            var Q19;
            Q19=makeQuery(id+"F6.imprint","IMPRINT",FACE,{"disambiguationData":[TD([[makeQuery(id+"F6.imprint","IMPRINT",EDGE,{"derivedFrom":sQuery(id+"F6.wireOp",EDGE,"E52")}),1.0]])]});
            var Q20;
            Q20=makeQuery(id+"F6.imprint","IMPRINT",FACE,{"disambiguationData":[TD([[makeQuery(id+"F6.imprint","IMPRINT",EDGE,{"derivedFrom":sQuery(id+"F6.wireOp",EDGE,"E92")}),1.0]])]});
            var Q21;
            Q21=makeQuery(id+"F6.imprint","IMPRINT",FACE,{"disambiguationData":[TD([[makeQuery(id+"F6.imprint","IMPRINT",EDGE,{"derivedFrom":sQuery(id+"F6.wireOp",EDGE,"E96")}),1.0]])]});
            var Q22;
            Q22=makeQuery(id+"F6.imprint","IMPRINT",FACE,{"disambiguationData":[TD([[makeQuery(id+"F6.imprint","IMPRINT",EDGE,{"derivedFrom":sQuery(id+"F6.wireOp",EDGE,"E100")}),1.0]])]});
            var Q23;
            Q23=makeQuery(id+"F6.imprint","IMPRINT",FACE,{"disambiguationData":[TD([[makeQuery(id+"F6.imprint","IMPRINT",EDGE,{"derivedFrom":sQuery(id+"F6.wireOp",EDGE,"E104")}),1.0]])]});
            var Q24;
            Q24=makeQuery(id+"F6.imprint","IMPRINT",FACE,{"disambiguationData":[TD([[makeQuery(id+"F6.imprint","IMPRINT",EDGE,{"derivedFrom":sQuery(id+"F6.wireOp",EDGE,"E108")}),1.0]])]});
            var Q25;
            Q25=makeQuery(id+"F6.imprint","IMPRINT",FACE,{"disambiguationData":[TD([[makeQuery(id+"F6.imprint","IMPRINT",EDGE,{"derivedFrom":sQuery(id+"F6.wireOp",EDGE,"E112")}),1.0]])]});
            var Q26;
            Q26=makeQuery(id+"F6.imprint","IMPRINT",FACE,{"disambiguationData":[TD([[makeQuery(id+"F6.imprint","IMPRINT",EDGE,{"derivedFrom":sQuery(id+"F6.wireOp",EDGE,"E116")}),1.0]])]});
            var Q27;
            Q27=makeQuery(id+"F6.imprint","IMPRINT",FACE,{"disambiguationData":[TD([[makeQuery(id+"F6.imprint","IMPRINT",EDGE,{"derivedFrom":sQuery(id+"F6.wireOp",EDGE,"E120")}),1.0]])]});
            var Q28;
            Q28=makeQuery(id+"F6.imprint","IMPRINT",FACE,{"disambiguationData":[TD([[makeQuery(id+"F6.imprint","IMPRINT",EDGE,{"derivedFrom":sQuery(id+"F6.wireOp",EDGE,"E124")}),1.0]])]});
            var Q29;
            Q29=makeQuery(id+"F6.imprint","IMPRINT",FACE,{"disambiguationData":[TD([[makeQuery(id+"F6.imprint","IMPRINT",EDGE,{"derivedFrom":sQuery(id+"F6.wireOp",EDGE,"E128")}),1.0]])]});
            var Q30;
            Q30=makeQuery(id+"F6.imprint","IMPRINT",FACE,{"disambiguationData":[TD([[makeQuery(id+"F6.imprint","IMPRINT",EDGE,{"derivedFrom":sQuery(id+"F6.wireOp",EDGE,"E168")}),1.0]])]});
            var Q31;
            Q31=makeQuery(id+"F6.imprint","IMPRINT",FACE,{"disambiguationData":[TD([[makeQuery(id+"F6.imprint","IMPRINT",EDGE,{"derivedFrom":sQuery(id+"F6.wireOp",EDGE,"E164")}),1.0]])]});
            var Q32;
            Q32=makeQuery(id+"F6.imprint","IMPRINT",FACE,{"disambiguationData":[TD([[makeQuery(id+"F6.imprint","IMPRINT",EDGE,{"derivedFrom":sQuery(id+"F6.wireOp",EDGE,"E160")}),1.0]])]});
            var Q33;
            Q33=makeQuery(id+"F6.imprint","IMPRINT",FACE,{"disambiguationData":[TD([[makeQuery(id+"F6.imprint","IMPRINT",EDGE,{"derivedFrom":sQuery(id+"F6.wireOp",EDGE,"E156")}),1.0]])]});
            var Q34;
            Q34=makeQuery(id+"F6.imprint","IMPRINT",FACE,{"disambiguationData":[TD([[makeQuery(id+"F6.imprint","IMPRINT",EDGE,{"derivedFrom":sQuery(id+"F6.wireOp",EDGE,"E152")}),1.0]])]});
            var Q35;
            Q35=makeQuery(id+"F6.imprint","IMPRINT",FACE,{"disambiguationData":[TD([[makeQuery(id+"F6.imprint","IMPRINT",EDGE,{"derivedFrom":sQuery(id+"F6.wireOp",EDGE,"E148")}),1.0]])]});
            var Q36;
            Q36=makeQuery(id+"F6.imprint","IMPRINT",FACE,{"disambiguationData":[TD([[makeQuery(id+"F6.imprint","IMPRINT",EDGE,{"derivedFrom":sQuery(id+"F6.wireOp",EDGE,"E144")}),1.0]])]});
            var Q37;
            Q37=makeQuery(id+"F6.imprint","IMPRINT",FACE,{"disambiguationData":[TD([[makeQuery(id+"F6.imprint","IMPRINT",EDGE,{"derivedFrom":sQuery(id+"F6.wireOp",EDGE,"E140")}),1.0]])]});
            var Q38;
            Q38=makeQuery(id+"F6.imprint","IMPRINT",FACE,{"disambiguationData":[TD([[makeQuery(id+"F6.imprint","IMPRINT",EDGE,{"derivedFrom":sQuery(id+"F6.wireOp",EDGE,"E136")}),1.0]])]});
            var Q39;
            Q39=makeQuery(id+"F6.imprint","IMPRINT",FACE,{"disambiguationData":[TD([[makeQuery(id+"F6.imprint","IMPRINT",EDGE,{"derivedFrom":sQuery(id+"F6.wireOp",EDGE,"E132")}),1.0]])]});
            var Q40;
            Q40=makeQuery(id+"F6.imprint","IMPRINT",FACE,{"disambiguationData":[TD([[makeQuery(id+"F6.imprint","IMPRINT",EDGE,{"derivedFrom":sQuery(id+"F6.wireOp",EDGE,"E172")}),1.0]])]});
            var Q41;
            Q41=makeQuery(id+"F6.imprint","IMPRINT",FACE,{"disambiguationData":[TD([[makeQuery(id+"F6.imprint","IMPRINT",EDGE,{"derivedFrom":sQuery(id+"F6.wireOp",EDGE,"E176")}),1.0]])]});
            var Q42;
            Q42=makeQuery(id+"F6.imprint","IMPRINT",FACE,{"disambiguationData":[TD([[makeQuery(id+"F6.imprint","IMPRINT",EDGE,{"derivedFrom":sQuery(id+"F6.wireOp",EDGE,"E180")}),1.0]])]});
            var Q43;
            Q43=makeQuery(id+"F6.imprint","IMPRINT",FACE,{"disambiguationData":[TD([[makeQuery(id+"F6.imprint","IMPRINT",EDGE,{"derivedFrom":sQuery(id+"F6.wireOp",EDGE,"E184")}),1.0]])]});
            var Q44;
            Q44=makeQuery(id+"F6.imprint","IMPRINT",FACE,{"disambiguationData":[TD([[makeQuery(id+"F6.imprint","IMPRINT",EDGE,{"derivedFrom":sQuery(id+"F6.wireOp",EDGE,"E188")}),1.0]])]});
            var Q45;
            Q45=makeQuery(id+"F6.imprint","IMPRINT",FACE,{"disambiguationData":[TD([[makeQuery(id+"F6.imprint","IMPRINT",EDGE,{"derivedFrom":sQuery(id+"F6.wireOp",EDGE,"E192")}),1.0]])]});
            var Q46;
            Q46=makeQuery(id+"F6.imprint","IMPRINT",FACE,{"disambiguationData":[TD([[makeQuery(id+"F6.imprint","IMPRINT",EDGE,{"derivedFrom":sQuery(id+"F6.wireOp",EDGE,"E196")}),1.0]])]});
            var Q47;
            Q47=makeQuery(id+"F6.imprint","IMPRINT",FACE,{"disambiguationData":[TD([[makeQuery(id+"F6.imprint","IMPRINT",EDGE,{"derivedFrom":sQuery(id+"F6.wireOp",EDGE,"E200")}),1.0]])]});
            var Q48;
            Q48=makeQuery(id+"F6.imprint","IMPRINT",FACE,{"disambiguationData":[TD([[makeQuery(id+"F6.imprint","IMPRINT",EDGE,{"derivedFrom":sQuery(id+"F6.wireOp",EDGE,"E204")}),1.0]])]});
            var Q49;
            Q49=makeQuery(id+"F6.imprint","IMPRINT",FACE,{"disambiguationData":[TD([[makeQuery(id+"F6.imprint","IMPRINT",EDGE,{"derivedFrom":sQuery(id+"F6.wireOp",EDGE,"E208")}),1.0]])]});
            var Q50;
            Q50=makeQuery(id+"F6.imprint","IMPRINT",FACE,{"disambiguationData":[TD([[makeQuery(id+"F6.imprint","IMPRINT",EDGE,{"derivedFrom":sQuery(id+"F6.wireOp",EDGE,"E248")}),1.0]])]});
            var Q51;
            Q51=makeQuery(id+"F6.imprint","IMPRINT",FACE,{"disambiguationData":[TD([[makeQuery(id+"F6.imprint","IMPRINT",EDGE,{"derivedFrom":sQuery(id+"F6.wireOp",EDGE,"E244")}),1.0]])]});
            var Q52;
            Q52=makeQuery(id+"F6.imprint","IMPRINT",FACE,{"disambiguationData":[TD([[makeQuery(id+"F6.imprint","IMPRINT",EDGE,{"derivedFrom":sQuery(id+"F6.wireOp",EDGE,"E240")}),1.0]])]});
            var Q53;
            Q53=makeQuery(id+"F6.imprint","IMPRINT",FACE,{"disambiguationData":[TD([[makeQuery(id+"F6.imprint","IMPRINT",EDGE,{"derivedFrom":sQuery(id+"F6.wireOp",EDGE,"E236")}),1.0]])]});
            var Q54;
            Q54=makeQuery(id+"F6.imprint","IMPRINT",FACE,{"disambiguationData":[TD([[makeQuery(id+"F6.imprint","IMPRINT",EDGE,{"derivedFrom":sQuery(id+"F6.wireOp",EDGE,"E232")}),1.0]])]});
            var Q55;
            Q55=makeQuery(id+"F6.imprint","IMPRINT",FACE,{"disambiguationData":[TD([[makeQuery(id+"F6.imprint","IMPRINT",EDGE,{"derivedFrom":sQuery(id+"F6.wireOp",EDGE,"E228")}),1.0]])]});
            var Q56;
            Q56=makeQuery(id+"F6.imprint","IMPRINT",FACE,{"disambiguationData":[TD([[makeQuery(id+"F6.imprint","IMPRINT",EDGE,{"derivedFrom":sQuery(id+"F6.wireOp",EDGE,"E224")}),1.0]])]});
            var Q57;
            Q57=makeQuery(id+"F6.imprint","IMPRINT",FACE,{"disambiguationData":[TD([[makeQuery(id+"F6.imprint","IMPRINT",EDGE,{"derivedFrom":sQuery(id+"F6.wireOp",EDGE,"E220")}),1.0]])]});
            var Q58;
            Q58=makeQuery(id+"F6.imprint","IMPRINT",FACE,{"disambiguationData":[TD([[makeQuery(id+"F6.imprint","IMPRINT",EDGE,{"derivedFrom":sQuery(id+"F6.wireOp",EDGE,"E216")}),1.0]])]});
            var Q59;
            Q59=makeQuery(id+"F6.imprint","IMPRINT",FACE,{"disambiguationData":[TD([[makeQuery(id+"F6.imprint","IMPRINT",EDGE,{"derivedFrom":sQuery(id+"F6.wireOp",EDGE,"E212")}),1.0]])]});
            var Q60;
            Q60=makeQuery(id+"F6.imprint","IMPRINT",FACE,{"disambiguationData":[TD([[makeQuery(id+"F6.imprint","IMPRINT",EDGE,{"derivedFrom":sQuery(id+"F6.wireOp",EDGE,"E252")}),1.0]])]});
            var Q61;
            Q61=makeQuery(id+"F6.imprint","IMPRINT",FACE,{"disambiguationData":[TD([[makeQuery(id+"F6.imprint","IMPRINT",EDGE,{"derivedFrom":sQuery(id+"F6.wireOp",EDGE,"E256")}),1.0]])]});
            var Q62;
            Q62=makeQuery(id+"F6.imprint","IMPRINT",FACE,{"disambiguationData":[TD([[makeQuery(id+"F6.imprint","IMPRINT",EDGE,{"derivedFrom":sQuery(id+"F6.wireOp",EDGE,"E260")}),1.0]])]});
            var Q63;
            Q63=makeQuery(id+"F6.imprint","IMPRINT",FACE,{"disambiguationData":[TD([[makeQuery(id+"F6.imprint","IMPRINT",EDGE,{"derivedFrom":sQuery(id+"F6.wireOp",EDGE,"E264")}),1.0]])]});
            var Q64;
            Q64=makeQuery(id+"F6.imprint","IMPRINT",FACE,{"disambiguationData":[TD([[makeQuery(id+"F6.imprint","IMPRINT",EDGE,{"derivedFrom":sQuery(id+"F6.wireOp",EDGE,"E268")}),1.0]])]});
            var Q65;
            Q65=makeQuery(id+"F6.imprint","IMPRINT",FACE,{"disambiguationData":[TD([[makeQuery(id+"F6.imprint","IMPRINT",EDGE,{"derivedFrom":sQuery(id+"F6.wireOp",EDGE,"E272")}),1.0]])]});
            var Q66;
            Q66=makeQuery(id+"F6.imprint","IMPRINT",FACE,{"disambiguationData":[TD([[makeQuery(id+"F6.imprint","IMPRINT",EDGE,{"derivedFrom":sQuery(id+"F6.wireOp",EDGE,"E276")}),1.0]])]});
            var Q67;
            Q67=makeQuery(id+"F6.imprint","IMPRINT",FACE,{"disambiguationData":[TD([[makeQuery(id+"F6.imprint","IMPRINT",EDGE,{"derivedFrom":sQuery(id+"F6.wireOp",EDGE,"E280")}),1.0]])]});
            var Q68;
            Q68=makeQuery(id+"F6.imprint","IMPRINT",FACE,{"disambiguationData":[TD([[makeQuery(id+"F6.imprint","IMPRINT",EDGE,{"derivedFrom":sQuery(id+"F6.wireOp",EDGE,"E284")}),1.0]])]});
            var Q69;
            Q69=makeQuery(id+"F6.imprint","IMPRINT",FACE,{"disambiguationData":[TD([[makeQuery(id+"F6.imprint","IMPRINT",EDGE,{"derivedFrom":sQuery(id+"F6.wireOp",EDGE,"E288")}),1.0]])]});
            var Q70;
            Q70=makeQuery(id+"F6.imprint","IMPRINT",FACE,{"disambiguationData":[TD([[makeQuery(id+"F6.imprint","IMPRINT",EDGE,{"derivedFrom":sQuery(id+"F6.wireOp",EDGE,"E328")}),1.0]])]});
            var Q71;
            Q71=makeQuery(id+"F6.imprint","IMPRINT",FACE,{"disambiguationData":[TD([[makeQuery(id+"F6.imprint","IMPRINT",EDGE,{"derivedFrom":sQuery(id+"F6.wireOp",EDGE,"E324")}),1.0]])]});
            var Q72;
            Q72=makeQuery(id+"F6.imprint","IMPRINT",FACE,{"disambiguationData":[TD([[makeQuery(id+"F6.imprint","IMPRINT",EDGE,{"derivedFrom":sQuery(id+"F6.wireOp",EDGE,"E320")}),1.0]])]});
            var Q73;
            Q73=makeQuery(id+"F6.imprint","IMPRINT",FACE,{"disambiguationData":[TD([[makeQuery(id+"F6.imprint","IMPRINT",EDGE,{"derivedFrom":sQuery(id+"F6.wireOp",EDGE,"E316")}),1.0]])]});
            var Q74;
            Q74=makeQuery(id+"F6.imprint","IMPRINT",FACE,{"disambiguationData":[TD([[makeQuery(id+"F6.imprint","IMPRINT",EDGE,{"derivedFrom":sQuery(id+"F6.wireOp",EDGE,"E312")}),1.0]])]});
            var Q75;
            Q75=makeQuery(id+"F6.imprint","IMPRINT",FACE,{"disambiguationData":[TD([[makeQuery(id+"F6.imprint","IMPRINT",EDGE,{"derivedFrom":sQuery(id+"F6.wireOp",EDGE,"E308")}),1.0]])]});
            var Q76;
            Q76=makeQuery(id+"F6.imprint","IMPRINT",FACE,{"disambiguationData":[TD([[makeQuery(id+"F6.imprint","IMPRINT",EDGE,{"derivedFrom":sQuery(id+"F6.wireOp",EDGE,"E304")}),1.0]])]});
            var Q77;
            Q77=makeQuery(id+"F6.imprint","IMPRINT",FACE,{"disambiguationData":[TD([[makeQuery(id+"F6.imprint","IMPRINT",EDGE,{"derivedFrom":sQuery(id+"F6.wireOp",EDGE,"E300")}),1.0]])]});
            var Q78;
            Q78=makeQuery(id+"F6.imprint","IMPRINT",FACE,{"disambiguationData":[TD([[makeQuery(id+"F6.imprint","IMPRINT",EDGE,{"derivedFrom":sQuery(id+"F6.wireOp",EDGE,"E296")}),1.0]])]});
            var Q79;
            Q79=makeQuery(id+"F6.imprint","IMPRINT",FACE,{"disambiguationData":[TD([[makeQuery(id+"F6.imprint","IMPRINT",EDGE,{"derivedFrom":sQuery(id+"F6.wireOp",EDGE,"E292")}),1.0]])]});
            var Q80;
            Q80=makeQuery(id+"F6.imprint","IMPRINT",FACE,{"disambiguationData":[TD([[makeQuery(id+"F6.imprint","IMPRINT",EDGE,{"derivedFrom":sQuery(id+"F6.wireOp",EDGE,"E332")}),1.0]])]});
            var Q81;
            Q81=makeQuery(id+"F6.imprint","IMPRINT",FACE,{"disambiguationData":[TD([[makeQuery(id+"F6.imprint","IMPRINT",EDGE,{"derivedFrom":sQuery(id+"F6.wireOp",EDGE,"E336")}),1.0]])]});
            var Q82;
            Q82=makeQuery(id+"F6.imprint","IMPRINT",FACE,{"disambiguationData":[TD([[makeQuery(id+"F6.imprint","IMPRINT",EDGE,{"derivedFrom":sQuery(id+"F6.wireOp",EDGE,"E340")}),1.0]])]});
            var Q83;
            Q83=makeQuery(id+"F6.imprint","IMPRINT",FACE,{"disambiguationData":[TD([[makeQuery(id+"F6.imprint","IMPRINT",EDGE,{"derivedFrom":sQuery(id+"F6.wireOp",EDGE,"E344")}),1.0]])]});
            var Q84;
            Q84=makeQuery(id+"F6.imprint","IMPRINT",FACE,{"disambiguationData":[TD([[makeQuery(id+"F6.imprint","IMPRINT",EDGE,{"derivedFrom":sQuery(id+"F6.wireOp",EDGE,"E348")}),1.0]])]});
            var Q85;
            Q85=makeQuery(id+"F6.imprint","IMPRINT",FACE,{"disambiguationData":[TD([[makeQuery(id+"F6.imprint","IMPRINT",EDGE,{"derivedFrom":sQuery(id+"F6.wireOp",EDGE,"E352")}),1.0]])]});
            var Q86;
            Q86=makeQuery(id+"F6.imprint","IMPRINT",FACE,{"disambiguationData":[TD([[makeQuery(id+"F6.imprint","IMPRINT",EDGE,{"derivedFrom":sQuery(id+"F6.wireOp",EDGE,"E356")}),1.0]])]});
            var Q87;
            Q87=makeQuery(id+"F6.imprint","IMPRINT",FACE,{"disambiguationData":[TD([[makeQuery(id+"F6.imprint","IMPRINT",EDGE,{"derivedFrom":sQuery(id+"F6.wireOp",EDGE,"E360")}),1.0]])]});
            var Q88;
            Q88=makeQuery(id+"F6.imprint","IMPRINT",FACE,{"disambiguationData":[TD([[makeQuery(id+"F6.imprint","IMPRINT",EDGE,{"derivedFrom":sQuery(id+"F6.wireOp",EDGE,"E364")}),1.0]])]});
            var Q89;
            Q89=makeQuery(id+"F6.imprint","IMPRINT",FACE,{"disambiguationData":[TD([[makeQuery(id+"F6.imprint","IMPRINT",EDGE,{"derivedFrom":sQuery(id+"F6.wireOp",EDGE,"E368")}),1.0]])]});
            var Q90;
            Q90=makeQuery(id+"F6.imprint","IMPRINT",FACE,{"disambiguationData":[TD([[makeQuery(id+"F6.imprint","IMPRINT",EDGE,{"derivedFrom":sQuery(id+"F6.wireOp",EDGE,"E408")}),1.0]])]});
            var Q91;
            Q91=makeQuery(id+"F6.imprint","IMPRINT",FACE,{"disambiguationData":[TD([[makeQuery(id+"F6.imprint","IMPRINT",EDGE,{"derivedFrom":sQuery(id+"F6.wireOp",EDGE,"E404")}),1.0]])]});
            var Q92;
            Q92=makeQuery(id+"F6.imprint","IMPRINT",FACE,{"disambiguationData":[TD([[makeQuery(id+"F6.imprint","IMPRINT",EDGE,{"derivedFrom":sQuery(id+"F6.wireOp",EDGE,"E400")}),1.0]])]});
            var Q93;
            Q93=makeQuery(id+"F6.imprint","IMPRINT",FACE,{"disambiguationData":[TD([[makeQuery(id+"F6.imprint","IMPRINT",EDGE,{"derivedFrom":sQuery(id+"F6.wireOp",EDGE,"E396")}),1.0]])]});
            var Q94;
            Q94=makeQuery(id+"F6.imprint","IMPRINT",FACE,{"disambiguationData":[TD([[makeQuery(id+"F6.imprint","IMPRINT",EDGE,{"derivedFrom":sQuery(id+"F6.wireOp",EDGE,"E392")}),1.0]])]});
            var Q95;
            Q95=makeQuery(id+"F6.imprint","IMPRINT",FACE,{"disambiguationData":[TD([[makeQuery(id+"F6.imprint","IMPRINT",EDGE,{"derivedFrom":sQuery(id+"F6.wireOp",EDGE,"E388")}),1.0]])]});
            var Q96;
            Q96=makeQuery(id+"F6.imprint","IMPRINT",FACE,{"disambiguationData":[TD([[makeQuery(id+"F6.imprint","IMPRINT",EDGE,{"derivedFrom":sQuery(id+"F6.wireOp",EDGE,"E384")}),1.0]])]});
            var Q97;
            Q97=makeQuery(id+"F6.imprint","IMPRINT",FACE,{"disambiguationData":[TD([[makeQuery(id+"F6.imprint","IMPRINT",EDGE,{"derivedFrom":sQuery(id+"F6.wireOp",EDGE,"E380")}),1.0]])]});
            var Q98;
            Q98=makeQuery(id+"F6.imprint","IMPRINT",FACE,{"disambiguationData":[TD([[makeQuery(id+"F6.imprint","IMPRINT",EDGE,{"derivedFrom":sQuery(id+"F6.wireOp",EDGE,"E376")}),1.0]])]});
            var Q99;
            Q99=makeQuery(id+"F6.imprint","IMPRINT",FACE,{"disambiguationData":[TD([[makeQuery(id+"F6.imprint","IMPRINT",EDGE,{"derivedFrom":sQuery(id+"F6.wireOp",EDGE,"E372")}),1.0]])]});
            var Q100;
            Q100=makeQuery(id+"F2.opExtrude","CAP_FACE",FACE,{"disambiguationData":[OSD([sQuery(id+"F1.wireOp",EDGE,"E0.bottom"),sQuery(id+"F1.wireOp",EDGE,"E0.top"),sQuery(id+"F1.wireOp",EDGE,"E0.left"),sQuery(id+"F1.wireOp",EDGE,"E0.right")])],"isStart":false});
            extrude(context, id + "F7", {"entities" : qUnion([Q0, Q1, Q2, Q3, Q4, Q5, Q6, Q7, Q8, Q9, Q10, Q11, Q12, Q13, Q14, Q15, Q16, Q17, Q18, Q19, Q20, Q21, Q22, Q23, Q24, Q25, Q26, Q27, Q28, Q29, Q30, Q31, Q32, Q33, Q34, Q35, Q36, Q37, Q38, Q39, Q40, Q41, Q42, Q43, Q44, Q45, Q46, Q47, Q48, Q49, Q50, Q51, Q52, Q53, Q54, Q55, Q56, Q57, Q58, Q59, Q60, Q61, Q62, Q63, Q64, Q65, Q66, Q67, Q68, Q69, Q70, Q71, Q72, Q73, Q74, Q75, Q76, Q77, Q78, Q79, Q80, Q81, Q82, Q83, Q84, Q85, Q86, Q87, Q88, Q89, Q90, Q91, Q92, Q93, Q94, Q95, Q96, Q97, Q98, Q99]), "operationType" : NewBodyOperationType.REMOVE, "endBound" : BoundingType.UP_TO_SURFACE, "oppositeDirection" : true, "endBoundEntityFace" : qUnion([Q100]), "depth" : 25 * mm});
        }
        {
            var Q0;
            Q0 = qSketchRegion(id + "F6", true);
            extrude(context, id + "F8", {"entities" : qUnion([Q0]), "operationType" : NewBodyOperationType.REMOVE, "oppositeDirection" : true, "depth" : getVariable(context, 'M6NutThickness')});
        }
    });
